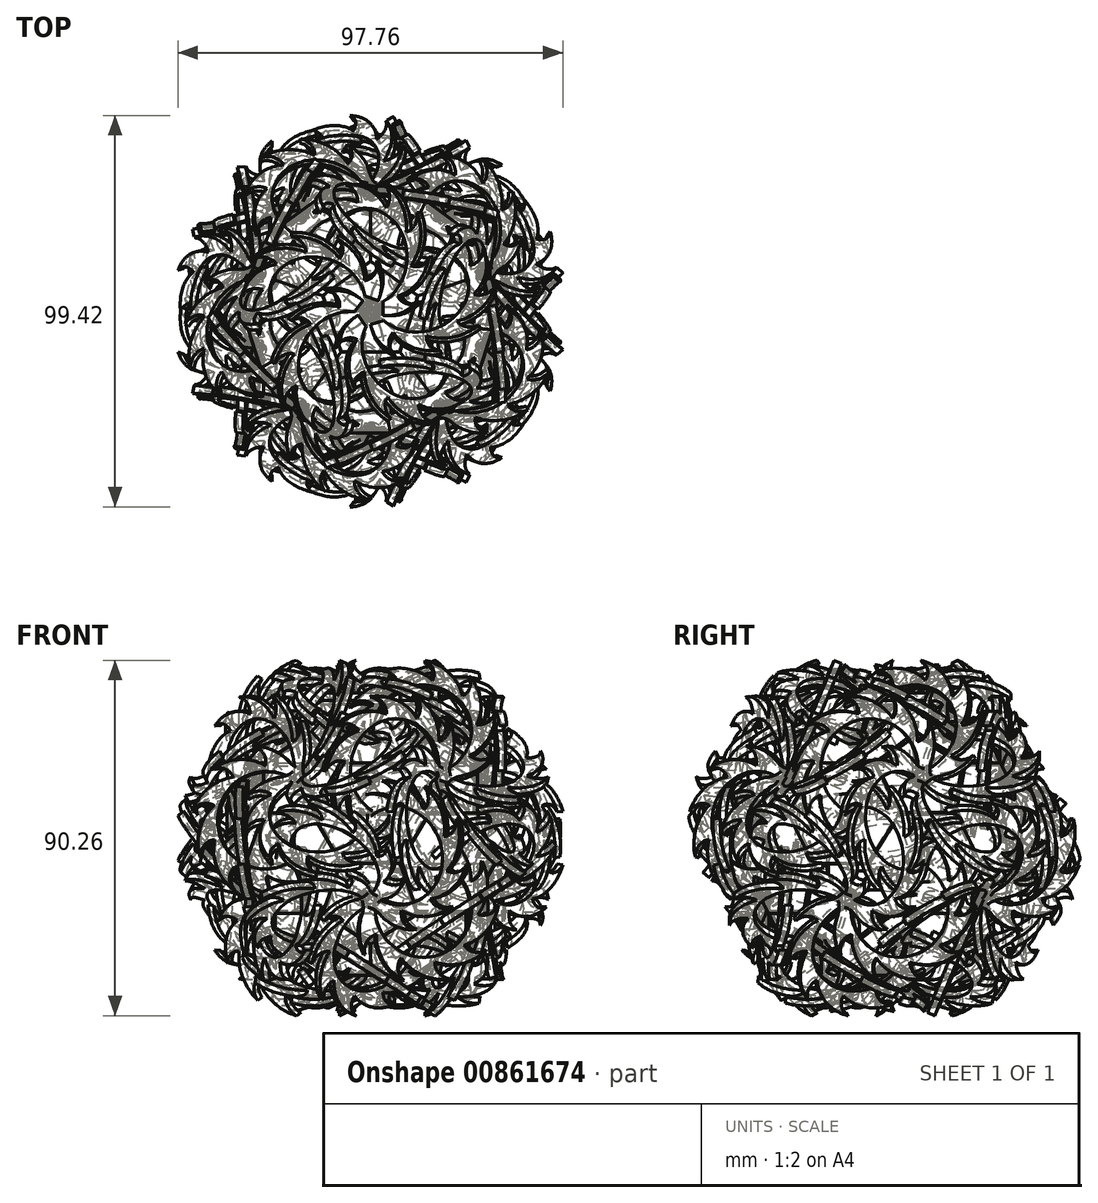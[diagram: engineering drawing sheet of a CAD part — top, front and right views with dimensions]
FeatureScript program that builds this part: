
annotation { "Feature Type Name" : "Feature", "Feature Type Description" : "" }
export const myFeature = defineFeature(function(context is Context, id is Id, definition is map)
    precondition{}
    {
        {
            var Q0;
            Q0=qCreatedBy(makeId("Top.planeOp"),FACE);
            var sketch = newSketch(context, id + "F0", { "sketchPlane" : qUnion([Q0])});
            skCircle(sketch, "E0.cCircle", {"center": v(0, 0) * mm, "radius": 10.32 * mm, "construction": true});
            skLineSegment(sketch, "E0.0", {"start": v(7.5, -10.32) * mm, "end": v(-7.5, -10.32) * mm});
            skLineSegment(sketch, "E0.1", {"start": v(-7.5, -10.32) * mm, "end": v(-12.14, 3.94) * mm});
            skLineSegment(sketch, "E0.2", {"start": v(-12.14, 3.94) * mm, "end": v(0, 12.76) * mm});
            skLineSegment(sketch, "E0.3", {"start": v(0, 12.76) * mm, "end": v(12.14, 3.94) * mm});
            skLineSegment(sketch, "E0.4", {"start": v(12.14, 3.94) * mm, "end": v(7.5, -10.32) * mm});
            skPoint(sketch, "E0.0.midPoint", {"position": v(0, -10.32) * mm});
            skLineSegment(sketch, "E1", {"start": v(0, 12.76) * mm, "end": v(0, -10.32) * mm});
            skSolve(sketch);
        }
        {
            var Q0;
            Q0=qCreatedBy(makeId("Top.planeOp"),FACE);
            var sketch = newSketch(context, id + "F1", { "sketchPlane" : qUnion([Q0])});
            skCircle(sketch, "E2.cCircle", {"center": v(22.17, -7.2) * mm, "radius": 13 * mm, "construction": true});
            skLineSegment(sketch, "E2.0", {"start": v(36.84, -4.09) * mm, "end": v(32.2, -18.35) * mm});
            skLineSegment(sketch, "E2.1", {"start": v(32.2, -18.35) * mm, "end": v(17.54, -21.47) * mm});
            skLineSegment(sketch, "E2.2", {"start": v(17.54, -21.47) * mm, "end": v(7.5, -10.32) * mm});
            skLineSegment(sketch, "E2.3", {"start": v(7.5, -10.32) * mm, "end": v(12.14, 3.94) * mm});
            skLineSegment(sketch, "E2.4", {"start": v(12.14, 3.94) * mm, "end": v(26.8, 7.06) * mm});
            skLineSegment(sketch, "E2.5", {"start": v(26.8, 7.06) * mm, "end": v(36.84, -4.09) * mm});
            skPoint(sketch, "E2.0.midPoint", {"position": v(34.53, -11.22) * mm});
            skSolve(sketch);
        }
        {
            var Q0;
            Q0=makeQuery(id+"F0.imprint","IMPRINT",FACE,{"disambiguationData":[TD([[makeQuery(id+"F0.imprint","IMPRINT",EDGE,{"derivedFrom":sQuery(id+"F0.wireOp",EDGE,"E0.0")}),-1.0]])]});
            extrude(context, id + "F2", {"entities" : qUnion([Q0]), "oppositeDirection" : true, "depth" : 1 * mm});
        }
        {
            var Q0;
            Q0=makeQuery(id+"F1.imprint","IMPRINT",FACE,{"disambiguationData":[TD([[makeQuery(id+"F1.imprint","IMPRINT",EDGE,{"derivedFrom":sQuery(id+"F1.wireOp",EDGE,"E2.0")}),-1.0]])]});
            extrude(context, id + "F3", {"entities" : qUnion([Q0]), "oppositeDirection" : true, "depth" : 1 * mm});
        }
        {
            var Q0;
            Q0=makeQuery(id+"F3.opExtrude","SWEPT_BODY",BODY,{"disambiguationData":[OSD([sQuery(id+"F1.wireOp",EDGE,"E2.0"),sQuery(id+"F1.wireOp",EDGE,"E2.1"),sQuery(id+"F1.wireOp",EDGE,"E2.2"),sQuery(id+"F1.wireOp",EDGE,"E2.3"),sQuery(id+"F1.wireOp",EDGE,"E2.4"),sQuery(id+"F1.wireOp",EDGE,"E2.5")])]});
            var Q1;
            Q1=makeQuery(id+"F2.opExtrude","CAP_EDGE",EDGE,{"disambiguationData":[OSD([sQuery(id+"F0.wireOp",EDGE,"E0.4")])],"isStart":true});
            transform(context, id + "F4", {"entities" : qUnion([Q0]), "transformType" : TransformType.ROTATION, "transformAxis" : qUnion([Q1]), "angle" : 37.38 * degree, "oppositeDirection" : true, "makeCopy" : false});
        }
        {
            var Q0;
            Q0=qCreatedBy(makeId("Right.planeOp"),FACE);
            var sketch = newSketch(context, id + "F5", { "sketchPlane" : qUnion([Q0])});
            skLineSegment(sketch, "E3", {"start": v(0, 0) * mm, "end": v(0, 7.73) * mm});
            skSolve(sketch);
        }
        {
            var Q0;
            Q0=makeQuery(id+"F3.opExtrude","SWEPT_BODY",BODY,{"disambiguationData":[OSD([sQuery(id+"F1.wireOp",EDGE,"E2.0"),sQuery(id+"F1.wireOp",EDGE,"E2.1"),sQuery(id+"F1.wireOp",EDGE,"E2.2"),sQuery(id+"F1.wireOp",EDGE,"E2.3"),sQuery(id+"F1.wireOp",EDGE,"E2.4"),sQuery(id+"F1.wireOp",EDGE,"E2.5")])]});
            var Q1;
            Q1=sQuery(id+"F5.wireOp",EDGE,"E3");
            circularPattern(context, id + "F6", {"entities" : qUnion([Q0]), "axis" : qUnion([Q1]), "angle" : 72 * degree, "instanceCount" : round(5)});
        }
        {
            var Q0;
            Q0=makeQuery(id+"F6.opPattern","COPY",FACE,{"derivedFrom":makeQuery(id+"F3.opExtrude","CAP_FACE",FACE,{"disambiguationData":[OSD([sQuery(id+"F1.wireOp",EDGE,"E2.0"),sQuery(id+"F1.wireOp",EDGE,"E2.1"),sQuery(id+"F1.wireOp",EDGE,"E2.2"),sQuery(id+"F1.wireOp",EDGE,"E2.3"),sQuery(id+"F1.wireOp",EDGE,"E2.4"),sQuery(id+"F1.wireOp",EDGE,"E2.5")])],"isStart":true}),"instanceName":"4"});
            var sketch = newSketch(context, id + "F7", { "sketchPlane" : qUnion([Q0])});
            skLineSegment(sketch, "E4", {"start": v(0, -34.18) * mm, "end": v(0, -8.2) * mm});
            skLineSegment(sketch, "E5", {"start": v(-15, -21.2) * mm, "end": v(15, -21.2) * mm});
            skCircle(sketch, "E6", {"center": v(0, -21.2) * mm, "radius": 3.24 * mm});
            skSolve(sketch);
        }
        {
            var Q0;
            Q0=qCreatedBy(makeId("Right.planeOp"),FACE);
            var sketch = newSketch(context, id + "F8", { "sketchPlane" : qUnion([Q0])});
            skArc(sketch, "E7.0", {"start": v(-1.37, 0) * mm, "mid": v(-18.04, 14.75) * mm, "end": v(-20.04, -7.42) * mm});
            skLineSegment(sketch, "E8", {"start": v(-20.04, -7.42) * mm, "end": v(-24.47, -10.8) * mm});
            skLineSegment(sketch, "E9", {"start": v(-1.37, 0) * mm, "end": v(0, 0) * mm});
            skArc(sketch, "E10", {"start": v(1.07, 1.27) * mm, "mid": v(3.46, 7.37) * mm, "end": v(2.5, 13.85) * mm});
            skArc(sketch, "E11", {"start": v(-0.8, 8.97) * mm, "mid": v(1.84, 10.74) * mm, "end": v(2.5, 13.85) * mm});
            skArc(sketch, "E12.1.0", {"start": v(-0.8, 8.97) * mm, "mid": v(-2.13, 15.94) * mm, "end": v(-6.98, 21.1) * mm});
            skArc(sketch, "E12.1.1", {"start": v(-6.75, 15.32) * mm, "mid": v(-5.72, 18.26) * mm, "end": v(-6.98, 21.1) * mm});
            skArc(sketch, "E12.2.0", {"start": v(-6.75, 15.32) * mm, "mid": v(-11.92, 20.18) * mm, "end": v(-18.89, 21.5) * mm});
            skArc(sketch, "E12.2.1", {"start": v(-15.3, 16.96) * mm, "mid": v(-16.2, 19.94) * mm, "end": v(-18.89, 21.5) * mm});
            skArc(sketch, "E12.3.0", {"start": v(-15.3, 16.96) * mm, "mid": v(-22.34, 17.85) * mm, "end": v(-28.75, 14.83) * mm});
            skArc(sketch, "E12.3.1", {"start": v(-23.18, 13.26) * mm, "mid": v(-25.66, 15.15) * mm, "end": v(-28.75, 14.83) * mm});
            skArc(sketch, "E12.4.0", {"start": v(-23.18, 13.26) * mm, "mid": v(-29.4, 9.84) * mm, "end": v(-32.81, 3.63) * mm});
            skArc(sketch, "E12.4.1", {"start": v(-27.38, 5.64) * mm, "mid": v(-30.5, 5.7) * mm, "end": v(-32.81, 3.63) * mm});
            skArc(sketch, "E12.5.0", {"start": v(-27.38, 5.64) * mm, "mid": v(-30.4, -0.78) * mm, "end": v(-29.51, -7.81) * mm});
            skArc(sketch, "E12.5.1", {"start": v(-26.3, -3) * mm, "mid": v(-28.86, -4.77) * mm, "end": v(-29.51, -7.81) * mm});
            skArc(sketch, "E12.6.0", {"start": v(-26.3, -3) * mm, "mid": v(-26.03, -7.06) * mm, "end": v(-24.49, -10.82) * mm});
            skArc(sketch, "E13", {"start": v(-24.49, -10.82) * mm, "mid": v(-20.56, -11.35) * mm, "end": v(-20.04, -7.42) * mm});
            skArc(sketch, "E14", {"start": v(-1.37, 0) * mm, "mid": v(1.27, -2.11) * mm, "end": v(1.07, 1.27) * mm});
            skSolve(sketch);
        }
        {
            var Q0;
            {var subQ2=sQuery(id+"F8.wireOp",EDGE,"E7.0");Q0=makeQuery(id+"F8.imprint","IMPRINT",FACE,{"disambiguationData":[TD([[makeQuery(id+"F8.imprint","IMPRINT",EDGE,{"derivedFrom":subQ2}),-1.0]])]});}
            extrude(context, id + "F9", {"entities" : qUnion([Q0]), "oppositeDirection" : true, "depth" : 2 * mm});
        }
        {
            var Q0;
            Q0=makeQuery(id+"F9.opExtrude","SWEPT_EDGE",EDGE,{"disambiguationData":[OSD([sQuery(id+"F8.wireOp",EDGE,"E10"),sQuery(id+"F8.wireOp",EDGE,"E14")])]});
            fillet(context, id + "F10", {"entities" : qUnion([Q0]), "radius" : 5 * mm, "tangentPropagation" : true, "allowEdgeOverflow" : false});
        }
        {
            var Q0;
            Q0=qCreatedBy(makeId("Right.planeOp"),FACE);
            var sketch = newSketch(context, id + "F11", { "sketchPlane" : qUnion([Q0])});
            skLineSegment(sketch, "E15", {"start": v(0, 0) * mm, "end": v(-20.65, -7.89) * mm});
            skLineSegment(sketch, "E16", {"start": v(0, 0) * mm, "end": v(0, 28.42) * mm});
            skSolve(sketch);
        }
        {
            var Q0;
            Q0=makeQuery(id+"F9.opExtrude","SWEPT_BODY",BODY,{"disambiguationData":[OSD([sQuery(id+"F8.wireOp",EDGE,"003f2e54-bd62-4f0b-a98e-8c36e71e2cf6"),sQuery(id+"F8.wireOp",EDGE,"8c729305-40a1-49fa-b790-4b99a3909bb6"),sQuery(id+"F8.wireOp",EDGE,"862a2a8f-3db7-4421-9c69-6ab2f53c4c24.1.0"),sQuery(id+"F8.wireOp",EDGE,"862a2a8f-3db7-4421-9c69-6ab2f53c4c24.1.1"),sQuery(id+"F8.wireOp",EDGE,"862a2a8f-3db7-4421-9c69-6ab2f53c4c24.2.0"),sQuery(id+"F8.wireOp",EDGE,"862a2a8f-3db7-4421-9c69-6ab2f53c4c24.2.1"),sQuery(id+"F8.wireOp",EDGE,"862a2a8f-3db7-4421-9c69-6ab2f53c4c24.3.0"),sQuery(id+"F8.wireOp",EDGE,"862a2a8f-3db7-4421-9c69-6ab2f53c4c24.3.1"),sQuery(id+"F8.wireOp",EDGE,"862a2a8f-3db7-4421-9c69-6ab2f53c4c24.4.0"),sQuery(id+"F8.wireOp",EDGE,"862a2a8f-3db7-4421-9c69-6ab2f53c4c24.4.1"),sQuery(id+"F8.wireOp",EDGE,"862a2a8f-3db7-4421-9c69-6ab2f53c4c24.5.0"),sQuery(id+"F8.wireOp",EDGE,"E7.0"),sQuery(id+"F8.wireOp",EDGE,"E8"),sQuery(id+"F8.wireOp",EDGE,"E9")])]});
            var Q1;
            Q1=sQuery(id+"F11.wireOp",EDGE,"E15");
            transform(context, id + "F12", {"entities" : qUnion([Q0]), "transformType" : TransformType.ROTATION, "transformAxis" : qUnion([Q1]), "angle" : 65 * degree, "makeCopy" : false});
        }
        {
            var Q0;
            Q0=makeQuery(id+"F9.opExtrude","SWEPT_BODY",BODY,{"disambiguationData":[OSD([sQuery(id+"F8.wireOp",EDGE,"003f2e54-bd62-4f0b-a98e-8c36e71e2cf6"),sQuery(id+"F8.wireOp",EDGE,"8c729305-40a1-49fa-b790-4b99a3909bb6"),sQuery(id+"F8.wireOp",EDGE,"862a2a8f-3db7-4421-9c69-6ab2f53c4c24.1.0"),sQuery(id+"F8.wireOp",EDGE,"862a2a8f-3db7-4421-9c69-6ab2f53c4c24.1.1"),sQuery(id+"F8.wireOp",EDGE,"862a2a8f-3db7-4421-9c69-6ab2f53c4c24.2.0"),sQuery(id+"F8.wireOp",EDGE,"862a2a8f-3db7-4421-9c69-6ab2f53c4c24.2.1"),sQuery(id+"F8.wireOp",EDGE,"862a2a8f-3db7-4421-9c69-6ab2f53c4c24.3.0"),sQuery(id+"F8.wireOp",EDGE,"862a2a8f-3db7-4421-9c69-6ab2f53c4c24.3.1"),sQuery(id+"F8.wireOp",EDGE,"862a2a8f-3db7-4421-9c69-6ab2f53c4c24.4.0"),sQuery(id+"F8.wireOp",EDGE,"862a2a8f-3db7-4421-9c69-6ab2f53c4c24.4.1"),sQuery(id+"F8.wireOp",EDGE,"862a2a8f-3db7-4421-9c69-6ab2f53c4c24.5.0"),sQuery(id+"F8.wireOp",EDGE,"E7.0"),sQuery(id+"F8.wireOp",EDGE,"E8"),sQuery(id+"F8.wireOp",EDGE,"E9")])]});
            var Q1;
            Q1=sQuery(id+"F11.wireOp",EDGE,"E16");
            circularPattern(context, id + "F13", {"entities" : qUnion([Q0]), "axis" : qUnion([Q1]), "angle" : 72 * degree, "instanceCount" : round(5)});
        }
        {
            var Q0;
            Q0=qCreatedBy(makeId("Right.planeOp"),FACE);
            var sketch = newSketch(context, id + "F14", { "sketchPlane" : qUnion([Q0])});
            skLineSegment(sketch, "E17.0", {"start": v(-30.97, -15.77) * mm, "end": v(-10.32, 0) * mm});
            skLineSegment(sketch, "E18", {"start": v(-20.65, -7.89) * mm, "end": v(-30.05, 4.42) * mm});
            skSolve(sketch);
        }
        {
            var Q0;
            Q0=makeQuery(id+"F9.opExtrude","SWEPT_BODY",BODY,{"disambiguationData":[OSD([sQuery(id+"F8.wireOp",EDGE,"003f2e54-bd62-4f0b-a98e-8c36e71e2cf6"),sQuery(id+"F8.wireOp",EDGE,"8c729305-40a1-49fa-b790-4b99a3909bb6"),sQuery(id+"F8.wireOp",EDGE,"862a2a8f-3db7-4421-9c69-6ab2f53c4c24.1.0"),sQuery(id+"F8.wireOp",EDGE,"862a2a8f-3db7-4421-9c69-6ab2f53c4c24.1.1"),sQuery(id+"F8.wireOp",EDGE,"862a2a8f-3db7-4421-9c69-6ab2f53c4c24.2.0"),sQuery(id+"F8.wireOp",EDGE,"862a2a8f-3db7-4421-9c69-6ab2f53c4c24.2.1"),sQuery(id+"F8.wireOp",EDGE,"862a2a8f-3db7-4421-9c69-6ab2f53c4c24.3.0"),sQuery(id+"F8.wireOp",EDGE,"862a2a8f-3db7-4421-9c69-6ab2f53c4c24.3.1"),sQuery(id+"F8.wireOp",EDGE,"862a2a8f-3db7-4421-9c69-6ab2f53c4c24.4.0"),sQuery(id+"F8.wireOp",EDGE,"862a2a8f-3db7-4421-9c69-6ab2f53c4c24.4.1"),sQuery(id+"F8.wireOp",EDGE,"862a2a8f-3db7-4421-9c69-6ab2f53c4c24.5.0"),sQuery(id+"F8.wireOp",EDGE,"E7.0"),sQuery(id+"F8.wireOp",EDGE,"E8"),sQuery(id+"F8.wireOp",EDGE,"E9")])]});
            var Q1;
            Q1=sQuery(id+"F14.wireOp",EDGE,"E18");
            circularPattern(context, id + "F15", {"entities" : qUnion([Q0]), "axis" : qUnion([Q1]), "angle" : 120 * degree, "instanceCount" : round(3)});
        }
        {
            var Q0;
            Q0=makeQuery(id+"F15.opPattern","COPY",BODY,{"derivedFrom":makeQuery(id+"F9.opExtrude","SWEPT_BODY",BODY,{"disambiguationData":[OSD([sQuery(id+"F8.wireOp",EDGE,"E7.0"),sQuery(id+"F8.wireOp",EDGE,"E10"),sQuery(id+"F8.wireOp",EDGE,"E11"),sQuery(id+"F8.wireOp",EDGE,"E12.1.0"),sQuery(id+"F8.wireOp",EDGE,"E12.1.1"),sQuery(id+"F8.wireOp",EDGE,"E12.2.0"),sQuery(id+"F8.wireOp",EDGE,"E12.2.1"),sQuery(id+"F8.wireOp",EDGE,"E12.3.0"),sQuery(id+"F8.wireOp",EDGE,"E12.3.1"),sQuery(id+"F8.wireOp",EDGE,"E12.4.0"),sQuery(id+"F8.wireOp",EDGE,"E12.4.1"),sQuery(id+"F8.wireOp",EDGE,"E12.5.0"),sQuery(id+"F8.wireOp",EDGE,"E12.5.1"),sQuery(id+"F8.wireOp",EDGE,"E12.6.0"),sQuery(id+"F8.wireOp",EDGE,"E13"),sQuery(id+"F8.wireOp",EDGE,"E14")])]}),"instanceName":"2"});
            var Q1;
            Q1=makeQuery(id+"F15.opPattern","COPY",BODY,{"derivedFrom":makeQuery(id+"F9.opExtrude","SWEPT_BODY",BODY,{"disambiguationData":[OSD([sQuery(id+"F8.wireOp",EDGE,"E7.0"),sQuery(id+"F8.wireOp",EDGE,"E10"),sQuery(id+"F8.wireOp",EDGE,"E11"),sQuery(id+"F8.wireOp",EDGE,"E12.1.0"),sQuery(id+"F8.wireOp",EDGE,"E12.1.1"),sQuery(id+"F8.wireOp",EDGE,"E12.2.0"),sQuery(id+"F8.wireOp",EDGE,"E12.2.1"),sQuery(id+"F8.wireOp",EDGE,"E12.3.0"),sQuery(id+"F8.wireOp",EDGE,"E12.3.1"),sQuery(id+"F8.wireOp",EDGE,"E12.4.0"),sQuery(id+"F8.wireOp",EDGE,"E12.4.1"),sQuery(id+"F8.wireOp",EDGE,"E12.5.0"),sQuery(id+"F8.wireOp",EDGE,"E12.5.1"),sQuery(id+"F8.wireOp",EDGE,"E12.6.0"),sQuery(id+"F8.wireOp",EDGE,"E13"),sQuery(id+"F8.wireOp",EDGE,"E14")])]}),"instanceName":"1"});
            var Q2;
            Q2=sQuery(id+"F11.wireOp",EDGE,"E16");
            circularPattern(context, id + "F16", {"entities" : qUnion([Q0, Q1]), "axis" : qUnion([Q2]), "angle" : 72 * degree, "instanceCount" : round(5)});
        }
        {
            var Q0;
            Q0=makeQuery(id+"F3.opExtrude","SWEPT_BODY",BODY,{"disambiguationData":[OSD([sQuery(id+"F1.wireOp",EDGE,"E2.0"),sQuery(id+"F1.wireOp",EDGE,"E2.1"),sQuery(id+"F1.wireOp",EDGE,"E2.2"),sQuery(id+"F1.wireOp",EDGE,"E2.3"),sQuery(id+"F1.wireOp",EDGE,"E2.4"),sQuery(id+"F1.wireOp",EDGE,"E2.5")])]});
            var Q1;
            Q1=makeQuery(id+"F16.opPattern","COPY",BODY,{"derivedFrom":makeQuery(id+"F15.opPattern","COPY",BODY,{"derivedFrom":makeQuery(id+"F9.opExtrude","SWEPT_BODY",BODY,{"disambiguationData":[OSD([sQuery(id+"F8.wireOp",EDGE,"E7.0"),sQuery(id+"F8.wireOp",EDGE,"E10"),sQuery(id+"F8.wireOp",EDGE,"E11"),sQuery(id+"F8.wireOp",EDGE,"E12.1.0"),sQuery(id+"F8.wireOp",EDGE,"E12.1.1"),sQuery(id+"F8.wireOp",EDGE,"E12.2.0"),sQuery(id+"F8.wireOp",EDGE,"E12.2.1"),sQuery(id+"F8.wireOp",EDGE,"E12.3.0"),sQuery(id+"F8.wireOp",EDGE,"E12.3.1"),sQuery(id+"F8.wireOp",EDGE,"E12.4.0"),sQuery(id+"F8.wireOp",EDGE,"E12.4.1"),sQuery(id+"F8.wireOp",EDGE,"E12.5.0"),sQuery(id+"F8.wireOp",EDGE,"E12.5.1"),sQuery(id+"F8.wireOp",EDGE,"E12.6.0"),sQuery(id+"F8.wireOp",EDGE,"E13"),sQuery(id+"F8.wireOp",EDGE,"E14")])]}),"instanceName":"1"}),"instanceName":"1"});
            var Q2;
            Q2=makeQuery(id+"F13.opPattern","COPY",BODY,{"derivedFrom":makeQuery(id+"F9.opExtrude","SWEPT_BODY",BODY,{"disambiguationData":[OSD([sQuery(id+"F8.wireOp",EDGE,"E7.0"),sQuery(id+"F8.wireOp",EDGE,"E10"),sQuery(id+"F8.wireOp",EDGE,"E11"),sQuery(id+"F8.wireOp",EDGE,"E12.1.0"),sQuery(id+"F8.wireOp",EDGE,"E12.1.1"),sQuery(id+"F8.wireOp",EDGE,"E12.2.0"),sQuery(id+"F8.wireOp",EDGE,"E12.2.1"),sQuery(id+"F8.wireOp",EDGE,"E12.3.0"),sQuery(id+"F8.wireOp",EDGE,"E12.3.1"),sQuery(id+"F8.wireOp",EDGE,"E12.4.0"),sQuery(id+"F8.wireOp",EDGE,"E12.4.1"),sQuery(id+"F8.wireOp",EDGE,"E12.5.0"),sQuery(id+"F8.wireOp",EDGE,"E12.5.1"),sQuery(id+"F8.wireOp",EDGE,"E12.6.0"),sQuery(id+"F8.wireOp",EDGE,"E13"),sQuery(id+"F8.wireOp",EDGE,"E14")])]}),"instanceName":"1"});
            var Q3;
            Q3=makeQuery(id+"F16.opPattern","COPY",BODY,{"derivedFrom":makeQuery(id+"F15.opPattern","COPY",BODY,{"derivedFrom":makeQuery(id+"F9.opExtrude","SWEPT_BODY",BODY,{"disambiguationData":[OSD([sQuery(id+"F8.wireOp",EDGE,"E7.0"),sQuery(id+"F8.wireOp",EDGE,"E10"),sQuery(id+"F8.wireOp",EDGE,"E11"),sQuery(id+"F8.wireOp",EDGE,"E12.1.0"),sQuery(id+"F8.wireOp",EDGE,"E12.1.1"),sQuery(id+"F8.wireOp",EDGE,"E12.2.0"),sQuery(id+"F8.wireOp",EDGE,"E12.2.1"),sQuery(id+"F8.wireOp",EDGE,"E12.3.0"),sQuery(id+"F8.wireOp",EDGE,"E12.3.1"),sQuery(id+"F8.wireOp",EDGE,"E12.4.0"),sQuery(id+"F8.wireOp",EDGE,"E12.4.1"),sQuery(id+"F8.wireOp",EDGE,"E12.5.0"),sQuery(id+"F8.wireOp",EDGE,"E12.5.1"),sQuery(id+"F8.wireOp",EDGE,"E12.6.0"),sQuery(id+"F8.wireOp",EDGE,"E13"),sQuery(id+"F8.wireOp",EDGE,"E14")])]}),"instanceName":"2"}),"instanceName":"1"});
            var Q4;
            Q4=sQuery(id+"F14.wireOp",EDGE,"E18");
            circularPattern(context, id + "F17", {"entities" : qUnion([Q0, Q1, Q2, Q3]), "axis" : qUnion([Q4]), "angle" : 120 * degree, "instanceCount" : 2, "oppositeDirection" : true});
        }
        {
            var Q0;
            Q0=makeQuery(id+"F2.opExtrude","SWEPT_BODY",BODY,{"disambiguationData":[OSD([sQuery(id+"F0.wireOp",EDGE,"E0.0"),sQuery(id+"F0.wireOp",EDGE,"E0.1"),sQuery(id+"F0.wireOp",EDGE,"E0.2"),sQuery(id+"F0.wireOp",EDGE,"E0.3"),sQuery(id+"F0.wireOp",EDGE,"E0.4")])]});
            var Q1;
            Q1=makeQuery(id+"F13.opPattern","COPY",BODY,{"derivedFrom":makeQuery(id+"F9.opExtrude","SWEPT_BODY",BODY,{"disambiguationData":[OSD([sQuery(id+"F8.wireOp",EDGE,"E7.0"),sQuery(id+"F8.wireOp",EDGE,"E10"),sQuery(id+"F8.wireOp",EDGE,"E11"),sQuery(id+"F8.wireOp",EDGE,"E12.1.0"),sQuery(id+"F8.wireOp",EDGE,"E12.1.1"),sQuery(id+"F8.wireOp",EDGE,"E12.2.0"),sQuery(id+"F8.wireOp",EDGE,"E12.2.1"),sQuery(id+"F8.wireOp",EDGE,"E12.3.0"),sQuery(id+"F8.wireOp",EDGE,"E12.3.1"),sQuery(id+"F8.wireOp",EDGE,"E12.4.0"),sQuery(id+"F8.wireOp",EDGE,"E12.4.1"),sQuery(id+"F8.wireOp",EDGE,"E12.5.0"),sQuery(id+"F8.wireOp",EDGE,"E12.5.1"),sQuery(id+"F8.wireOp",EDGE,"E12.6.0"),sQuery(id+"F8.wireOp",EDGE,"E13"),sQuery(id+"F8.wireOp",EDGE,"E14")])]}),"instanceName":"2"});
            var Q2;
            Q2=makeQuery(id+"F13.opPattern","COPY",BODY,{"derivedFrom":makeQuery(id+"F9.opExtrude","SWEPT_BODY",BODY,{"disambiguationData":[OSD([sQuery(id+"F8.wireOp",EDGE,"E7.0"),sQuery(id+"F8.wireOp",EDGE,"E10"),sQuery(id+"F8.wireOp",EDGE,"E11"),sQuery(id+"F8.wireOp",EDGE,"E12.1.0"),sQuery(id+"F8.wireOp",EDGE,"E12.1.1"),sQuery(id+"F8.wireOp",EDGE,"E12.2.0"),sQuery(id+"F8.wireOp",EDGE,"E12.2.1"),sQuery(id+"F8.wireOp",EDGE,"E12.3.0"),sQuery(id+"F8.wireOp",EDGE,"E12.3.1"),sQuery(id+"F8.wireOp",EDGE,"E12.4.0"),sQuery(id+"F8.wireOp",EDGE,"E12.4.1"),sQuery(id+"F8.wireOp",EDGE,"E12.5.0"),sQuery(id+"F8.wireOp",EDGE,"E12.5.1"),sQuery(id+"F8.wireOp",EDGE,"E12.6.0"),sQuery(id+"F8.wireOp",EDGE,"E13"),sQuery(id+"F8.wireOp",EDGE,"E14")])]}),"instanceName":"3"});
            var Q3;
            Q3=sQuery(id+"F14.wireOp",EDGE,"E18");
            circularPattern(context, id + "F18", {"entities" : qUnion([Q0, Q1, Q2]), "axis" : qUnion([Q3]), "angle" : 120 * degree, "instanceCount" : round(3)});
        }
        {
            var Q0;
            Q0=makeQuery(id+"F18.opPattern","COPY",FACE,{"derivedFrom":makeQuery(id+"F2.opExtrude","CAP_FACE",FACE,{"disambiguationData":[OSD([sQuery(id+"F0.wireOp",EDGE,"E0.0"),sQuery(id+"F0.wireOp",EDGE,"E0.1"),sQuery(id+"F0.wireOp",EDGE,"E0.2"),sQuery(id+"F0.wireOp",EDGE,"E0.3"),sQuery(id+"F0.wireOp",EDGE,"E0.4")])],"isStart":true}),"instanceName":"1"});
            var sketch = newSketch(context, id + "F19", { "sketchPlane" : qUnion([Q0])});
            skLineSegment(sketch, "E19", {"start": v(-1.3, -23.63) * mm, "end": v(-19.97, -37.2) * mm});
            skLineSegment(sketch, "E20", {"start": v(-19.97, -22.2) * mm, "end": v(-1.3, -35.77) * mm});
            skSolve(sketch);
        }
        {
            var Q0;
            Q0=sQuery(id+"F19.wireOp",VERTEX,"E19.end");
            var Q1;
            Q1=sQuery(id+"F19.wireOp",VERTEX,"E19.start");
            var Q2;
            Q2=sQuery(id+"F14.wireOp",VERTEX,"E18.end");
            cPlane(context, id + "F20", {"entities" : qUnion([Q0, Q1, Q2]), "cplaneType" : CPlaneType.THREE_POINT, "offset" : 150 * mm, "width" : 150 * mm, "height" : 150 * mm});
        }
        {
            var Q0;
            Q0=qCreatedBy(id+"F20.planeOp",FACE);
            var sketch = newSketch(context, id + "F21", { "sketchPlane" : qUnion([Q0])});
            skLineSegment(sketch, "E21.0", {"start": v(23.59, 6.27) * mm, "end": v(41.93, -7.75) * mm});
            skLineSegment(sketch, "E21.1", {"start": v(34.92, -2.4) * mm, "end": v(29.26, 1.94) * mm});
            skLineSegment(sketch, "E22", {"start": v(31.8, 0) * mm, "end": v(33.22, 1.87) * mm});
            skLineSegment(sketch, "E23", {"start": v(33.22, 1.87) * mm, "end": v(37.58, 7.58) * mm});
            skSolve(sketch);
        }
        {
            var Q0;
            Q0=makeQuery(id+"F17.opPattern","COPY",BODY,{"derivedFrom":makeQuery(id+"F3.opExtrude","SWEPT_BODY",BODY,{"disambiguationData":[OSD([sQuery(id+"F1.wireOp",EDGE,"E2.0"),sQuery(id+"F1.wireOp",EDGE,"E2.1"),sQuery(id+"F1.wireOp",EDGE,"E2.2"),sQuery(id+"F1.wireOp",EDGE,"E2.3"),sQuery(id+"F1.wireOp",EDGE,"E2.4"),sQuery(id+"F1.wireOp",EDGE,"E2.5")])]}),"instanceName":"1"});
            var Q1;
            Q1=makeQuery(id+"F17.opPattern","COPY",BODY,{"derivedFrom":makeQuery(id+"F13.opPattern","COPY",BODY,{"derivedFrom":makeQuery(id+"F9.opExtrude","SWEPT_BODY",BODY,{"disambiguationData":[OSD([sQuery(id+"F8.wireOp",EDGE,"E7.0"),sQuery(id+"F8.wireOp",EDGE,"E10"),sQuery(id+"F8.wireOp",EDGE,"E11"),sQuery(id+"F8.wireOp",EDGE,"E12.1.0"),sQuery(id+"F8.wireOp",EDGE,"E12.1.1"),sQuery(id+"F8.wireOp",EDGE,"E12.2.0"),sQuery(id+"F8.wireOp",EDGE,"E12.2.1"),sQuery(id+"F8.wireOp",EDGE,"E12.3.0"),sQuery(id+"F8.wireOp",EDGE,"E12.3.1"),sQuery(id+"F8.wireOp",EDGE,"E12.4.0"),sQuery(id+"F8.wireOp",EDGE,"E12.4.1"),sQuery(id+"F8.wireOp",EDGE,"E12.5.0"),sQuery(id+"F8.wireOp",EDGE,"E12.5.1"),sQuery(id+"F8.wireOp",EDGE,"E12.6.0"),sQuery(id+"F8.wireOp",EDGE,"E13"),sQuery(id+"F8.wireOp",EDGE,"E14")])]}),"instanceName":"1"}),"instanceName":"1"});
            var Q2;
            Q2=makeQuery(id+"F17.opPattern","COPY",BODY,{"derivedFrom":makeQuery(id+"F16.opPattern","COPY",BODY,{"derivedFrom":makeQuery(id+"F15.opPattern","COPY",BODY,{"derivedFrom":makeQuery(id+"F9.opExtrude","SWEPT_BODY",BODY,{"disambiguationData":[OSD([sQuery(id+"F8.wireOp",EDGE,"E7.0"),sQuery(id+"F8.wireOp",EDGE,"E10"),sQuery(id+"F8.wireOp",EDGE,"E11"),sQuery(id+"F8.wireOp",EDGE,"E12.1.0"),sQuery(id+"F8.wireOp",EDGE,"E12.1.1"),sQuery(id+"F8.wireOp",EDGE,"E12.2.0"),sQuery(id+"F8.wireOp",EDGE,"E12.2.1"),sQuery(id+"F8.wireOp",EDGE,"E12.3.0"),sQuery(id+"F8.wireOp",EDGE,"E12.3.1"),sQuery(id+"F8.wireOp",EDGE,"E12.4.0"),sQuery(id+"F8.wireOp",EDGE,"E12.4.1"),sQuery(id+"F8.wireOp",EDGE,"E12.5.0"),sQuery(id+"F8.wireOp",EDGE,"E12.5.1"),sQuery(id+"F8.wireOp",EDGE,"E12.6.0"),sQuery(id+"F8.wireOp",EDGE,"E13"),sQuery(id+"F8.wireOp",EDGE,"E14")])]}),"instanceName":"2"}),"instanceName":"1"}),"instanceName":"1"});
            var Q3;
            Q3=makeQuery(id+"F17.opPattern","COPY",BODY,{"derivedFrom":makeQuery(id+"F16.opPattern","COPY",BODY,{"derivedFrom":makeQuery(id+"F15.opPattern","COPY",BODY,{"derivedFrom":makeQuery(id+"F9.opExtrude","SWEPT_BODY",BODY,{"disambiguationData":[OSD([sQuery(id+"F8.wireOp",EDGE,"E7.0"),sQuery(id+"F8.wireOp",EDGE,"E10"),sQuery(id+"F8.wireOp",EDGE,"E11"),sQuery(id+"F8.wireOp",EDGE,"E12.1.0"),sQuery(id+"F8.wireOp",EDGE,"E12.1.1"),sQuery(id+"F8.wireOp",EDGE,"E12.2.0"),sQuery(id+"F8.wireOp",EDGE,"E12.2.1"),sQuery(id+"F8.wireOp",EDGE,"E12.3.0"),sQuery(id+"F8.wireOp",EDGE,"E12.3.1"),sQuery(id+"F8.wireOp",EDGE,"E12.4.0"),sQuery(id+"F8.wireOp",EDGE,"E12.4.1"),sQuery(id+"F8.wireOp",EDGE,"E12.5.0"),sQuery(id+"F8.wireOp",EDGE,"E12.5.1"),sQuery(id+"F8.wireOp",EDGE,"E12.6.0"),sQuery(id+"F8.wireOp",EDGE,"E13"),sQuery(id+"F8.wireOp",EDGE,"E14")])]}),"instanceName":"1"}),"instanceName":"1"}),"instanceName":"1"});
            var Q4;
            Q4=sQuery(id+"F21.wireOp",EDGE,"E22");
            circularPattern(context, id + "F22", {"entities" : qUnion([Q0, Q1, Q2, Q3]), "axis" : qUnion([Q4]), "angle" : 72 * degree, "instanceCount" : round(3), "oppositeDirection" : true});
        }
        {
            var Q0;
            Q0=makeQuery(id+"F18.opPattern","COPY",FACE,{"derivedFrom":makeQuery(id+"F2.opExtrude","CAP_FACE",FACE,{"disambiguationData":[OSD([sQuery(id+"F0.wireOp",EDGE,"E0.0"),sQuery(id+"F0.wireOp",EDGE,"E0.1"),sQuery(id+"F0.wireOp",EDGE,"E0.2"),sQuery(id+"F0.wireOp",EDGE,"E0.3"),sQuery(id+"F0.wireOp",EDGE,"E0.4")])],"isStart":true}),"instanceName":"2"});
            var sketch = newSketch(context, id + "F23", { "sketchPlane" : qUnion([Q0])});
            skLineSegment(sketch, "E24", {"start": v(1.3, -23.63) * mm, "end": v(19.97, -37.2) * mm});
            skLineSegment(sketch, "E25", {"start": v(5.7, -41.83) * mm, "end": v(12.84, -19.88) * mm});
            skSolve(sketch);
        }
        {
            var Q0;
            Q0=sQuery(id+"F23.wireOp",VERTEX,"E24.end");
            var Q1;
            Q1=sQuery(id+"F23.wireOp",VERTEX,"E24.start");
            var Q2;
            Q2=sQuery(id+"F14.wireOp",VERTEX,"E18.end");
            cPlane(context, id + "F24", {"entities" : qUnion([Q0, Q1, Q2]), "cplaneType" : CPlaneType.THREE_POINT, "offset" : 150 * mm, "width" : 150 * mm, "height" : 150 * mm});
        }
        {
            var Q0;
            Q0=qCreatedBy(id+"F24.planeOp",FACE);
            var sketch = newSketch(context, id + "F25", { "sketchPlane" : qUnion([Q0])});
            skLineSegment(sketch, "E26.0", {"start": v(23.59, 6.27) * mm, "end": v(41.93, -7.75) * mm});
            skLineSegment(sketch, "E26.1", {"start": v(34.92, -2.4) * mm, "end": v(29.26, 1.94) * mm});
            skLineSegment(sketch, "E27", {"start": v(31.8, 0) * mm, "end": v(36.23, 5.8) * mm});
            skSolve(sketch);
        }
        {
            var Q0;
            Q0=makeQuery(id+"F3.opExtrude","SWEPT_BODY",BODY,{"disambiguationData":[OSD([sQuery(id+"F1.wireOp",EDGE,"E2.0"),sQuery(id+"F1.wireOp",EDGE,"E2.1"),sQuery(id+"F1.wireOp",EDGE,"E2.2"),sQuery(id+"F1.wireOp",EDGE,"E2.3"),sQuery(id+"F1.wireOp",EDGE,"E2.4"),sQuery(id+"F1.wireOp",EDGE,"E2.5")])]});
            var Q1;
            Q1=makeQuery(id+"F16.opPattern","COPY",BODY,{"derivedFrom":makeQuery(id+"F15.opPattern","COPY",BODY,{"derivedFrom":makeQuery(id+"F9.opExtrude","SWEPT_BODY",BODY,{"disambiguationData":[OSD([sQuery(id+"F8.wireOp",EDGE,"E7.0"),sQuery(id+"F8.wireOp",EDGE,"E10"),sQuery(id+"F8.wireOp",EDGE,"E11"),sQuery(id+"F8.wireOp",EDGE,"E12.1.0"),sQuery(id+"F8.wireOp",EDGE,"E12.1.1"),sQuery(id+"F8.wireOp",EDGE,"E12.2.0"),sQuery(id+"F8.wireOp",EDGE,"E12.2.1"),sQuery(id+"F8.wireOp",EDGE,"E12.3.0"),sQuery(id+"F8.wireOp",EDGE,"E12.3.1"),sQuery(id+"F8.wireOp",EDGE,"E12.4.0"),sQuery(id+"F8.wireOp",EDGE,"E12.4.1"),sQuery(id+"F8.wireOp",EDGE,"E12.5.0"),sQuery(id+"F8.wireOp",EDGE,"E12.5.1"),sQuery(id+"F8.wireOp",EDGE,"E12.6.0"),sQuery(id+"F8.wireOp",EDGE,"E13"),sQuery(id+"F8.wireOp",EDGE,"E14")])]}),"instanceName":"2"}),"instanceName":"1"});
            var Q2;
            Q2=makeQuery(id+"F13.opPattern","COPY",BODY,{"derivedFrom":makeQuery(id+"F9.opExtrude","SWEPT_BODY",BODY,{"disambiguationData":[OSD([sQuery(id+"F8.wireOp",EDGE,"E7.0"),sQuery(id+"F8.wireOp",EDGE,"E10"),sQuery(id+"F8.wireOp",EDGE,"E11"),sQuery(id+"F8.wireOp",EDGE,"E12.1.0"),sQuery(id+"F8.wireOp",EDGE,"E12.1.1"),sQuery(id+"F8.wireOp",EDGE,"E12.2.0"),sQuery(id+"F8.wireOp",EDGE,"E12.2.1"),sQuery(id+"F8.wireOp",EDGE,"E12.3.0"),sQuery(id+"F8.wireOp",EDGE,"E12.3.1"),sQuery(id+"F8.wireOp",EDGE,"E12.4.0"),sQuery(id+"F8.wireOp",EDGE,"E12.4.1"),sQuery(id+"F8.wireOp",EDGE,"E12.5.0"),sQuery(id+"F8.wireOp",EDGE,"E12.5.1"),sQuery(id+"F8.wireOp",EDGE,"E12.6.0"),sQuery(id+"F8.wireOp",EDGE,"E13"),sQuery(id+"F8.wireOp",EDGE,"E14")])]}),"instanceName":"1"});
            var Q3;
            Q3=makeQuery(id+"F16.opPattern","COPY",BODY,{"derivedFrom":makeQuery(id+"F15.opPattern","COPY",BODY,{"derivedFrom":makeQuery(id+"F9.opExtrude","SWEPT_BODY",BODY,{"disambiguationData":[OSD([sQuery(id+"F8.wireOp",EDGE,"E7.0"),sQuery(id+"F8.wireOp",EDGE,"E10"),sQuery(id+"F8.wireOp",EDGE,"E11"),sQuery(id+"F8.wireOp",EDGE,"E12.1.0"),sQuery(id+"F8.wireOp",EDGE,"E12.1.1"),sQuery(id+"F8.wireOp",EDGE,"E12.2.0"),sQuery(id+"F8.wireOp",EDGE,"E12.2.1"),sQuery(id+"F8.wireOp",EDGE,"E12.3.0"),sQuery(id+"F8.wireOp",EDGE,"E12.3.1"),sQuery(id+"F8.wireOp",EDGE,"E12.4.0"),sQuery(id+"F8.wireOp",EDGE,"E12.4.1"),sQuery(id+"F8.wireOp",EDGE,"E12.5.0"),sQuery(id+"F8.wireOp",EDGE,"E12.5.1"),sQuery(id+"F8.wireOp",EDGE,"E12.6.0"),sQuery(id+"F8.wireOp",EDGE,"E13"),sQuery(id+"F8.wireOp",EDGE,"E14")])]}),"instanceName":"1"}),"instanceName":"1"});
            var Q4;
            Q4=sQuery(id+"F25.wireOp",EDGE,"E27");
            circularPattern(context, id + "F26", {"entities" : qUnion([Q0, Q1, Q2, Q3]), "axis" : qUnion([Q4]), "angle" : 72 * degree, "instanceCount" : round(3), "oppositeDirection" : true});
        }
        {
            var Q0;
            Q0=makeQuery(id+"F17.opPattern","COPY",FACE,{"derivedFrom":makeQuery(id+"F3.opExtrude","CAP_FACE",FACE,{"disambiguationData":[OSD([sQuery(id+"F1.wireOp",EDGE,"E2.0"),sQuery(id+"F1.wireOp",EDGE,"E2.1"),sQuery(id+"F1.wireOp",EDGE,"E2.2"),sQuery(id+"F1.wireOp",EDGE,"E2.3"),sQuery(id+"F1.wireOp",EDGE,"E2.4"),sQuery(id+"F1.wireOp",EDGE,"E2.5")])],"isStart":true}),"instanceName":"1"});
            var sketch = newSketch(context, id + "F27", { "sketchPlane" : qUnion([Q0])});
            skLineSegment(sketch, "E28", {"start": v(0, -47.28) * mm, "end": v(0, -21.3) * mm});
            skSolve(sketch);
        }
        {
            var Q0;
            Q0=qCreatedBy(makeId("Right.planeOp"),FACE);
            var sketch = newSketch(context, id + "F28", { "sketchPlane" : qUnion([Q0])});
            skLineSegment(sketch, "E29.0", {"start": v(-35.84, -41.3) * mm, "end": v(-30.97, -15.77) * mm});
            skLineSegment(sketch, "E30", {"start": v(-33.4, -28.53) * mm, "end": v(-47.6, -25.82) * mm});
            skSolve(sketch);
        }
        {
            var Q0;
            Q0=makeQuery(id+"F18.opPattern","COPY",BODY,{"derivedFrom":makeQuery(id+"F2.opExtrude","SWEPT_BODY",BODY,{"disambiguationData":[OSD([sQuery(id+"F0.wireOp",EDGE,"E0.0"),sQuery(id+"F0.wireOp",EDGE,"E0.1"),sQuery(id+"F0.wireOp",EDGE,"E0.2"),sQuery(id+"F0.wireOp",EDGE,"E0.3"),sQuery(id+"F0.wireOp",EDGE,"E0.4")])]}),"instanceName":"2"});
            var Q1;
            Q1=sQuery(id+"F28.wireOp",EDGE,"E30");
            circularPattern(context, id + "F29", {"entities" : qUnion([Q0]), "axis" : qUnion([Q1]), "angle" : 120 * degree, "instanceCount" : 2, "oppositeDirection" : true});
        }
        {
            var Q0;
            Q0=makeQuery(id+"F29.opPattern","COPY",FACE,{"derivedFrom":makeQuery(id+"F18.opPattern","COPY",FACE,{"derivedFrom":makeQuery(id+"F2.opExtrude","CAP_FACE",FACE,{"disambiguationData":[OSD([sQuery(id+"F0.wireOp",EDGE,"E0.0"),sQuery(id+"F0.wireOp",EDGE,"E0.1"),sQuery(id+"F0.wireOp",EDGE,"E0.2"),sQuery(id+"F0.wireOp",EDGE,"E0.3"),sQuery(id+"F0.wireOp",EDGE,"E0.4")])],"isStart":true}),"instanceName":"2"}),"instanceName":"1"});
            var sketch = newSketch(context, id + "F30", { "sketchPlane" : qUnion([Q0])});
            skLineSegment(sketch, "E31", {"start": v(0, -43.99) * mm, "end": v(0, -31.23) * mm});
            skLineSegment(sketch, "E32", {"start": v(-12.14, -35.17) * mm, "end": v(9.82, -28.04) * mm});
            skPoint(sketch, "E33.orphan", {"position": v(0, -20.9) * mm});
            skSolve(sketch);
        }
        {
            var Q0;
            Q0=qCreatedBy(makeId("Right.planeOp"),FACE);
            var sketch = newSketch(context, id + "F31", { "sketchPlane" : qUnion([Q0])});
            skLineSegment(sketch, "E34.0", {"start": v(-25.52, -61.94) * mm, "end": v(-31.23, -50.52) * mm});
            skLineSegment(sketch, "E35", {"start": v(-31.23, -50.52) * mm, "end": v(-51.07, -60.45) * mm});
            skSolve(sketch);
        }
        {
            var Q0;
            Q0=makeQuery(id+"F26.opPattern","COPY",BODY,{"derivedFrom":makeQuery(id+"F3.opExtrude","SWEPT_BODY",BODY,{"disambiguationData":[OSD([sQuery(id+"F1.wireOp",EDGE,"E2.0"),sQuery(id+"F1.wireOp",EDGE,"E2.1"),sQuery(id+"F1.wireOp",EDGE,"E2.2"),sQuery(id+"F1.wireOp",EDGE,"E2.3"),sQuery(id+"F1.wireOp",EDGE,"E2.4"),sQuery(id+"F1.wireOp",EDGE,"E2.5")])]}),"instanceName":"2"});
            var Q1;
            Q1=makeQuery(id+"F26.opPattern","COPY",BODY,{"derivedFrom":makeQuery(id+"F16.opPattern","COPY",BODY,{"derivedFrom":makeQuery(id+"F15.opPattern","COPY",BODY,{"derivedFrom":makeQuery(id+"F9.opExtrude","SWEPT_BODY",BODY,{"disambiguationData":[OSD([sQuery(id+"F8.wireOp",EDGE,"E7.0"),sQuery(id+"F8.wireOp",EDGE,"E10"),sQuery(id+"F8.wireOp",EDGE,"E11"),sQuery(id+"F8.wireOp",EDGE,"E12.1.0"),sQuery(id+"F8.wireOp",EDGE,"E12.1.1"),sQuery(id+"F8.wireOp",EDGE,"E12.2.0"),sQuery(id+"F8.wireOp",EDGE,"E12.2.1"),sQuery(id+"F8.wireOp",EDGE,"E12.3.0"),sQuery(id+"F8.wireOp",EDGE,"E12.3.1"),sQuery(id+"F8.wireOp",EDGE,"E12.4.0"),sQuery(id+"F8.wireOp",EDGE,"E12.4.1"),sQuery(id+"F8.wireOp",EDGE,"E12.5.0"),sQuery(id+"F8.wireOp",EDGE,"E12.5.1"),sQuery(id+"F8.wireOp",EDGE,"E12.6.0"),sQuery(id+"F8.wireOp",EDGE,"E13"),sQuery(id+"F8.wireOp",EDGE,"E14")])]}),"instanceName":"2"}),"instanceName":"1"}),"instanceName":"2"});
            var Q2;
            Q2=makeQuery(id+"F26.opPattern","COPY",BODY,{"derivedFrom":makeQuery(id+"F13.opPattern","COPY",BODY,{"derivedFrom":makeQuery(id+"F9.opExtrude","SWEPT_BODY",BODY,{"disambiguationData":[OSD([sQuery(id+"F8.wireOp",EDGE,"E7.0"),sQuery(id+"F8.wireOp",EDGE,"E10"),sQuery(id+"F8.wireOp",EDGE,"E11"),sQuery(id+"F8.wireOp",EDGE,"E12.1.0"),sQuery(id+"F8.wireOp",EDGE,"E12.1.1"),sQuery(id+"F8.wireOp",EDGE,"E12.2.0"),sQuery(id+"F8.wireOp",EDGE,"E12.2.1"),sQuery(id+"F8.wireOp",EDGE,"E12.3.0"),sQuery(id+"F8.wireOp",EDGE,"E12.3.1"),sQuery(id+"F8.wireOp",EDGE,"E12.4.0"),sQuery(id+"F8.wireOp",EDGE,"E12.4.1"),sQuery(id+"F8.wireOp",EDGE,"E12.5.0"),sQuery(id+"F8.wireOp",EDGE,"E12.5.1"),sQuery(id+"F8.wireOp",EDGE,"E12.6.0"),sQuery(id+"F8.wireOp",EDGE,"E13"),sQuery(id+"F8.wireOp",EDGE,"E14")])]}),"instanceName":"1"}),"instanceName":"2"});
            var Q3;
            Q3=makeQuery(id+"F18.opPattern","COPY",BODY,{"derivedFrom":makeQuery(id+"F13.opPattern","COPY",BODY,{"derivedFrom":makeQuery(id+"F9.opExtrude","SWEPT_BODY",BODY,{"disambiguationData":[OSD([sQuery(id+"F8.wireOp",EDGE,"E7.0"),sQuery(id+"F8.wireOp",EDGE,"E10"),sQuery(id+"F8.wireOp",EDGE,"E11"),sQuery(id+"F8.wireOp",EDGE,"E12.1.0"),sQuery(id+"F8.wireOp",EDGE,"E12.1.1"),sQuery(id+"F8.wireOp",EDGE,"E12.2.0"),sQuery(id+"F8.wireOp",EDGE,"E12.2.1"),sQuery(id+"F8.wireOp",EDGE,"E12.3.0"),sQuery(id+"F8.wireOp",EDGE,"E12.3.1"),sQuery(id+"F8.wireOp",EDGE,"E12.4.0"),sQuery(id+"F8.wireOp",EDGE,"E12.4.1"),sQuery(id+"F8.wireOp",EDGE,"E12.5.0"),sQuery(id+"F8.wireOp",EDGE,"E12.5.1"),sQuery(id+"F8.wireOp",EDGE,"E12.6.0"),sQuery(id+"F8.wireOp",EDGE,"E13"),sQuery(id+"F8.wireOp",EDGE,"E14")])]}),"instanceName":"2"}),"instanceName":"2"});
            var Q4;
            Q4=sQuery(id+"F31.wireOp",EDGE,"E35");
            circularPattern(context, id + "F32", {"entities" : qUnion([Q0, Q1, Q2, Q3]), "axis" : qUnion([Q4]), "angle" : 72 * degree, "instanceCount" : round(3), "oppositeDirection" : true});
        }
        {
            var Q0;
            Q0=makeQuery(id+"F6.opPattern","COPY",FACE,{"derivedFrom":makeQuery(id+"F3.opExtrude","CAP_FACE",FACE,{"disambiguationData":[OSD([sQuery(id+"F1.wireOp",EDGE,"E2.0"),sQuery(id+"F1.wireOp",EDGE,"E2.1"),sQuery(id+"F1.wireOp",EDGE,"E2.2"),sQuery(id+"F1.wireOp",EDGE,"E2.3"),sQuery(id+"F1.wireOp",EDGE,"E2.4"),sQuery(id+"F1.wireOp",EDGE,"E2.5")])],"isStart":true}),"instanceName":"2"});
            var sketch = newSketch(context, id + "F33", { "sketchPlane" : qUnion([Q0])});
            skLineSegment(sketch, "E36", {"start": v(-4.1, 7.1) * mm, "end": v(-17.1, 29.6) * mm});
            skSolve(sketch);
        }
        {
            var Q0;
            Q0=sQuery(id+"F33.wireOp",VERTEX,"E36.end");
            var Q1;
            Q1=sQuery(id+"F33.wireOp",VERTEX,"E36.start");
            var Q2;
            Q2=sQuery(id+"F11.wireOp",VERTEX,"E16.end");
            cPlane(context, id + "F34", {"entities" : qUnion([Q0, Q1, Q2]), "cplaneType" : CPlaneType.THREE_POINT, "offset" : 150 * mm, "width" : 150 * mm, "height" : 150 * mm});
        }
        {
            var Q0;
            Q0=qCreatedBy(id+"F34.planeOp",FACE);
            var sketch = newSketch(context, id + "F35", { "sketchPlane" : qUnion([Q0])});
            skLineSegment(sketch, "E37.0", {"start": v(10.32, 0) * mm, "end": v(30.97, -15.77) * mm});
            skLineSegment(sketch, "E38", {"start": v(20.65, -7.89) * mm, "end": v(38.57, 15.58) * mm});
            skSolve(sketch);
        }
        {
            var Q0;
            Q0=makeQuery(id+"F2.opExtrude","SWEPT_BODY",BODY,{"disambiguationData":[OSD([sQuery(id+"F0.wireOp",EDGE,"E0.0"),sQuery(id+"F0.wireOp",EDGE,"E0.1"),sQuery(id+"F0.wireOp",EDGE,"E0.2"),sQuery(id+"F0.wireOp",EDGE,"E0.3"),sQuery(id+"F0.wireOp",EDGE,"E0.4")])]});
            var Q1;
            Q1=sQuery(id+"F35.wireOp",EDGE,"E38");
            circularPattern(context, id + "F36", {"entities" : qUnion([Q0]), "axis" : qUnion([Q1]), "angle" : 120 * degree, "instanceCount" : round(3), "oppositeDirection" : true});
        }
        {
            var Q0;
            Q0=makeQuery(id+"F36.opPattern","COPY",FACE,{"derivedFrom":makeQuery(id+"F2.opExtrude","CAP_FACE",FACE,{"disambiguationData":[OSD([sQuery(id+"F0.wireOp",EDGE,"E0.0"),sQuery(id+"F0.wireOp",EDGE,"E0.1"),sQuery(id+"F0.wireOp",EDGE,"E0.2"),sQuery(id+"F0.wireOp",EDGE,"E0.3"),sQuery(id+"F0.wireOp",EDGE,"E0.4")])],"isStart":true}),"instanceName":"1"});
            var sketch = newSketch(context, id + "F37", { "sketchPlane" : qUnion([Q0])});
            skLineSegment(sketch, "E39", {"start": v(-4.5, -30.9) * mm, "end": v(1.45, -42.2) * mm});
            skPoint(sketch, "E40.orphan", {"position": v(-9.3, -21.76) * mm});
            skSolve(sketch);
        }
        {
            var Q0;
            Q0=sQuery(id+"F37.wireOp",VERTEX,"E39.end");
            var Q1;
            Q1=sQuery(id+"F37.wireOp",VERTEX,"E39.start");
            var Q2;
            Q2=sQuery(id+"F35.wireOp",VERTEX,"E38.end");
            cPlane(context, id + "F38", {"entities" : qUnion([Q0, Q1, Q2]), "cplaneType" : CPlaneType.THREE_POINT, "offset" : 150 * mm, "width" : 150 * mm, "height" : 150 * mm});
        }
        {
            var Q0;
            Q0=qCreatedBy(id+"F38.planeOp",FACE);
            var sketch = newSketch(context, id + "F39", { "sketchPlane" : qUnion([Q0])});
            skLineSegment(sketch, "E41.0", {"start": v(29.7, -11.34) * mm, "end": v(36.4, -22.2) * mm});
            skLineSegment(sketch, "E42", {"start": v(29.7, -11.34) * mm, "end": v(58.3, 6.33) * mm});
            skSolve(sketch);
        }
        {
            var Q0;
            Q0=makeQuery(id+"F22.opPattern","COPY",BODY,{"derivedFrom":makeQuery(id+"F17.opPattern","COPY",BODY,{"derivedFrom":makeQuery(id+"F3.opExtrude","SWEPT_BODY",BODY,{"disambiguationData":[OSD([sQuery(id+"F1.wireOp",EDGE,"E2.0"),sQuery(id+"F1.wireOp",EDGE,"E2.1"),sQuery(id+"F1.wireOp",EDGE,"E2.2"),sQuery(id+"F1.wireOp",EDGE,"E2.3"),sQuery(id+"F1.wireOp",EDGE,"E2.4"),sQuery(id+"F1.wireOp",EDGE,"E2.5")])]}),"instanceName":"1"}),"instanceName":"2"});
            var Q1;
            Q1=makeQuery(id+"F22.opPattern","COPY",BODY,{"derivedFrom":makeQuery(id+"F17.opPattern","COPY",BODY,{"derivedFrom":makeQuery(id+"F16.opPattern","COPY",BODY,{"derivedFrom":makeQuery(id+"F15.opPattern","COPY",BODY,{"derivedFrom":makeQuery(id+"F9.opExtrude","SWEPT_BODY",BODY,{"disambiguationData":[OSD([sQuery(id+"F8.wireOp",EDGE,"E7.0"),sQuery(id+"F8.wireOp",EDGE,"E10"),sQuery(id+"F8.wireOp",EDGE,"E11"),sQuery(id+"F8.wireOp",EDGE,"E12.1.0"),sQuery(id+"F8.wireOp",EDGE,"E12.1.1"),sQuery(id+"F8.wireOp",EDGE,"E12.2.0"),sQuery(id+"F8.wireOp",EDGE,"E12.2.1"),sQuery(id+"F8.wireOp",EDGE,"E12.3.0"),sQuery(id+"F8.wireOp",EDGE,"E12.3.1"),sQuery(id+"F8.wireOp",EDGE,"E12.4.0"),sQuery(id+"F8.wireOp",EDGE,"E12.4.1"),sQuery(id+"F8.wireOp",EDGE,"E12.5.0"),sQuery(id+"F8.wireOp",EDGE,"E12.5.1"),sQuery(id+"F8.wireOp",EDGE,"E12.6.0"),sQuery(id+"F8.wireOp",EDGE,"E13"),sQuery(id+"F8.wireOp",EDGE,"E14")])]}),"instanceName":"2"}),"instanceName":"1"}),"instanceName":"1"}),"instanceName":"2"});
            var Q2;
            Q2=makeQuery(id+"F22.opPattern","COPY",BODY,{"derivedFrom":makeQuery(id+"F17.opPattern","COPY",BODY,{"derivedFrom":makeQuery(id+"F13.opPattern","COPY",BODY,{"derivedFrom":makeQuery(id+"F9.opExtrude","SWEPT_BODY",BODY,{"disambiguationData":[OSD([sQuery(id+"F8.wireOp",EDGE,"E7.0"),sQuery(id+"F8.wireOp",EDGE,"E10"),sQuery(id+"F8.wireOp",EDGE,"E11"),sQuery(id+"F8.wireOp",EDGE,"E12.1.0"),sQuery(id+"F8.wireOp",EDGE,"E12.1.1"),sQuery(id+"F8.wireOp",EDGE,"E12.2.0"),sQuery(id+"F8.wireOp",EDGE,"E12.2.1"),sQuery(id+"F8.wireOp",EDGE,"E12.3.0"),sQuery(id+"F8.wireOp",EDGE,"E12.3.1"),sQuery(id+"F8.wireOp",EDGE,"E12.4.0"),sQuery(id+"F8.wireOp",EDGE,"E12.4.1"),sQuery(id+"F8.wireOp",EDGE,"E12.5.0"),sQuery(id+"F8.wireOp",EDGE,"E12.5.1"),sQuery(id+"F8.wireOp",EDGE,"E12.6.0"),sQuery(id+"F8.wireOp",EDGE,"E13"),sQuery(id+"F8.wireOp",EDGE,"E14")])]}),"instanceName":"1"}),"instanceName":"1"}),"instanceName":"2"});
            var Q3;
            Q3=makeQuery(id+"F18.opPattern","COPY",BODY,{"derivedFrom":makeQuery(id+"F13.opPattern","COPY",BODY,{"derivedFrom":makeQuery(id+"F9.opExtrude","SWEPT_BODY",BODY,{"disambiguationData":[OSD([sQuery(id+"F8.wireOp",EDGE,"E7.0"),sQuery(id+"F8.wireOp",EDGE,"E10"),sQuery(id+"F8.wireOp",EDGE,"E11"),sQuery(id+"F8.wireOp",EDGE,"E12.1.0"),sQuery(id+"F8.wireOp",EDGE,"E12.1.1"),sQuery(id+"F8.wireOp",EDGE,"E12.2.0"),sQuery(id+"F8.wireOp",EDGE,"E12.2.1"),sQuery(id+"F8.wireOp",EDGE,"E12.3.0"),sQuery(id+"F8.wireOp",EDGE,"E12.3.1"),sQuery(id+"F8.wireOp",EDGE,"E12.4.0"),sQuery(id+"F8.wireOp",EDGE,"E12.4.1"),sQuery(id+"F8.wireOp",EDGE,"E12.5.0"),sQuery(id+"F8.wireOp",EDGE,"E12.5.1"),sQuery(id+"F8.wireOp",EDGE,"E12.6.0"),sQuery(id+"F8.wireOp",EDGE,"E13"),sQuery(id+"F8.wireOp",EDGE,"E14")])]}),"instanceName":"2"}),"instanceName":"1"});
            var Q4;
            Q4=sQuery(id+"F39.wireOp",EDGE,"E42");
            circularPattern(context, id + "F40", {"entities" : qUnion([Q0, Q1, Q2, Q3]), "axis" : qUnion([Q4]), "angle" : 72 * degree, "instanceCount" : round(3), "oppositeDirection" : true});
        }
        {
            var Q0;
            Q0=makeQuery(id+"F36.opPattern","COPY",FACE,{"derivedFrom":makeQuery(id+"F2.opExtrude","CAP_FACE",FACE,{"disambiguationData":[OSD([sQuery(id+"F0.wireOp",EDGE,"E0.0"),sQuery(id+"F0.wireOp",EDGE,"E0.1"),sQuery(id+"F0.wireOp",EDGE,"E0.2"),sQuery(id+"F0.wireOp",EDGE,"E0.3"),sQuery(id+"F0.wireOp",EDGE,"E0.4")])],"isStart":true}),"instanceName":"2"});
            var sketch = newSketch(context, id + "F41", { "sketchPlane" : qUnion([Q0])});
            skLineSegment(sketch, "E43", {"start": v(0, -18.47) * mm, "end": v(0, -31.23) * mm});
            skPoint(sketch, "E44.orphan", {"position": v(0, -41.55) * mm});
            skSolve(sketch);
        }
        {
            var Q0;
            Q0=sQuery(id+"F41.wireOp",VERTEX,"E43.end");
            var Q1;
            Q1=sQuery(id+"F41.wireOp",VERTEX,"E43.start");
            var Q2;
            Q2=sQuery(id+"F11.wireOp",VERTEX,"E16.end");
            cPlane(context, id + "F42", {"entities" : qUnion([Q0, Q1, Q2]), "cplaneType" : CPlaneType.THREE_POINT, "offset" : 150 * mm, "width" : 150 * mm, "height" : 150 * mm});
        }
        {
            var Q0;
            Q0=qCreatedBy(id+"F42.planeOp",FACE);
            var sketch = newSketch(context, id + "F43", { "sketchPlane" : qUnion([Q0])});
            skLineSegment(sketch, "E45.0", {"start": v(-25.52, -7.89) * mm, "end": v(-31.23, -19.3) * mm});
            skLineSegment(sketch, "E46", {"start": v(-31.23, -19.3) * mm, "end": v(-78.41, 4.3) * mm});
            skSolve(sketch);
        }
        {
            var Q0;
            Q0=makeQuery(id+"F40.opPattern","COPY",BODY,{"derivedFrom":makeQuery(id+"F22.opPattern","COPY",BODY,{"derivedFrom":makeQuery(id+"F17.opPattern","COPY",BODY,{"derivedFrom":makeQuery(id+"F3.opExtrude","SWEPT_BODY",BODY,{"disambiguationData":[OSD([sQuery(id+"F1.wireOp",EDGE,"E2.0"),sQuery(id+"F1.wireOp",EDGE,"E2.1"),sQuery(id+"F1.wireOp",EDGE,"E2.2"),sQuery(id+"F1.wireOp",EDGE,"E2.3"),sQuery(id+"F1.wireOp",EDGE,"E2.4"),sQuery(id+"F1.wireOp",EDGE,"E2.5")])]}),"instanceName":"1"}),"instanceName":"2"}),"instanceName":"2"});
            var Q1;
            Q1=makeQuery(id+"F40.opPattern","COPY",BODY,{"derivedFrom":makeQuery(id+"F22.opPattern","COPY",BODY,{"derivedFrom":makeQuery(id+"F17.opPattern","COPY",BODY,{"derivedFrom":makeQuery(id+"F13.opPattern","COPY",BODY,{"derivedFrom":makeQuery(id+"F9.opExtrude","SWEPT_BODY",BODY,{"disambiguationData":[OSD([sQuery(id+"F8.wireOp",EDGE,"E7.0"),sQuery(id+"F8.wireOp",EDGE,"E10"),sQuery(id+"F8.wireOp",EDGE,"E11"),sQuery(id+"F8.wireOp",EDGE,"E12.1.0"),sQuery(id+"F8.wireOp",EDGE,"E12.1.1"),sQuery(id+"F8.wireOp",EDGE,"E12.2.0"),sQuery(id+"F8.wireOp",EDGE,"E12.2.1"),sQuery(id+"F8.wireOp",EDGE,"E12.3.0"),sQuery(id+"F8.wireOp",EDGE,"E12.3.1"),sQuery(id+"F8.wireOp",EDGE,"E12.4.0"),sQuery(id+"F8.wireOp",EDGE,"E12.4.1"),sQuery(id+"F8.wireOp",EDGE,"E12.5.0"),sQuery(id+"F8.wireOp",EDGE,"E12.5.1"),sQuery(id+"F8.wireOp",EDGE,"E12.6.0"),sQuery(id+"F8.wireOp",EDGE,"E13"),sQuery(id+"F8.wireOp",EDGE,"E14")])]}),"instanceName":"1"}),"instanceName":"1"}),"instanceName":"2"}),"instanceName":"2"});
            var Q2;
            Q2=makeQuery(id+"F40.opPattern","COPY",BODY,{"derivedFrom":makeQuery(id+"F18.opPattern","COPY",BODY,{"derivedFrom":makeQuery(id+"F13.opPattern","COPY",BODY,{"derivedFrom":makeQuery(id+"F9.opExtrude","SWEPT_BODY",BODY,{"disambiguationData":[OSD([sQuery(id+"F8.wireOp",EDGE,"E7.0"),sQuery(id+"F8.wireOp",EDGE,"E10"),sQuery(id+"F8.wireOp",EDGE,"E11"),sQuery(id+"F8.wireOp",EDGE,"E12.1.0"),sQuery(id+"F8.wireOp",EDGE,"E12.1.1"),sQuery(id+"F8.wireOp",EDGE,"E12.2.0"),sQuery(id+"F8.wireOp",EDGE,"E12.2.1"),sQuery(id+"F8.wireOp",EDGE,"E12.3.0"),sQuery(id+"F8.wireOp",EDGE,"E12.3.1"),sQuery(id+"F8.wireOp",EDGE,"E12.4.0"),sQuery(id+"F8.wireOp",EDGE,"E12.4.1"),sQuery(id+"F8.wireOp",EDGE,"E12.5.0"),sQuery(id+"F8.wireOp",EDGE,"E12.5.1"),sQuery(id+"F8.wireOp",EDGE,"E12.6.0"),sQuery(id+"F8.wireOp",EDGE,"E13"),sQuery(id+"F8.wireOp",EDGE,"E14")])]}),"instanceName":"2"}),"instanceName":"1"}),"instanceName":"2"});
            var Q3;
            Q3=makeQuery(id+"F40.opPattern","COPY",BODY,{"derivedFrom":makeQuery(id+"F22.opPattern","COPY",BODY,{"derivedFrom":makeQuery(id+"F17.opPattern","COPY",BODY,{"derivedFrom":makeQuery(id+"F16.opPattern","COPY",BODY,{"derivedFrom":makeQuery(id+"F15.opPattern","COPY",BODY,{"derivedFrom":makeQuery(id+"F9.opExtrude","SWEPT_BODY",BODY,{"disambiguationData":[OSD([sQuery(id+"F8.wireOp",EDGE,"E7.0"),sQuery(id+"F8.wireOp",EDGE,"E10"),sQuery(id+"F8.wireOp",EDGE,"E11"),sQuery(id+"F8.wireOp",EDGE,"E12.1.0"),sQuery(id+"F8.wireOp",EDGE,"E12.1.1"),sQuery(id+"F8.wireOp",EDGE,"E12.2.0"),sQuery(id+"F8.wireOp",EDGE,"E12.2.1"),sQuery(id+"F8.wireOp",EDGE,"E12.3.0"),sQuery(id+"F8.wireOp",EDGE,"E12.3.1"),sQuery(id+"F8.wireOp",EDGE,"E12.4.0"),sQuery(id+"F8.wireOp",EDGE,"E12.4.1"),sQuery(id+"F8.wireOp",EDGE,"E12.5.0"),sQuery(id+"F8.wireOp",EDGE,"E12.5.1"),sQuery(id+"F8.wireOp",EDGE,"E12.6.0"),sQuery(id+"F8.wireOp",EDGE,"E13"),sQuery(id+"F8.wireOp",EDGE,"E14")])]}),"instanceName":"2"}),"instanceName":"1"}),"instanceName":"1"}),"instanceName":"2"}),"instanceName":"2"});
            var Q4;
            Q4=sQuery(id+"F43.wireOp",EDGE,"E46");
            circularPattern(context, id + "F44", {"entities" : qUnion([Q0, Q1, Q2, Q3]), "axis" : qUnion([Q4]), "angle" : 72 * degree, "instanceCount" : round(3), "oppositeDirection" : true});
        }
        {
            var Q0;
            Q0=makeQuery(id+"F40.opPattern","COPY",FACE,{"derivedFrom":makeQuery(id+"F22.opPattern","COPY",FACE,{"derivedFrom":makeQuery(id+"F17.opPattern","COPY",FACE,{"derivedFrom":makeQuery(id+"F3.opExtrude","CAP_FACE",FACE,{"disambiguationData":[OSD([sQuery(id+"F1.wireOp",EDGE,"E2.0"),sQuery(id+"F1.wireOp",EDGE,"E2.1"),sQuery(id+"F1.wireOp",EDGE,"E2.2"),sQuery(id+"F1.wireOp",EDGE,"E2.3"),sQuery(id+"F1.wireOp",EDGE,"E2.4"),sQuery(id+"F1.wireOp",EDGE,"E2.5")])],"isStart":true}),"instanceName":"1"}),"instanceName":"2"}),"instanceName":"1"});
            var sketch = newSketch(context, id + "F45", { "sketchPlane" : qUnion([Q0])});
            skLineSegment(sketch, "E47", {"start": v(1.3, -21.26) * mm, "end": v(2.09, -34.23) * mm});
            skSolve(sketch);
        }
        {
            var Q0;
            Q0=sQuery(id+"F45.wireOp",VERTEX,"E47.end");
            var Q1;
            Q1=sQuery(id+"F45.wireOp",VERTEX,"E47.start");
            var Q2;
            Q2=makeQuery(id+"F6.opPattern","COPY",VERTEX,{"derivedFrom":makeQuery(id+"F3.opExtrude","CAP_VERTEX",VERTEX,{"disambiguationData":[OSD([sQuery(id+"F1.wireOp",EDGE,"E2.1"),sQuery(id+"F1.wireOp",EDGE,"E2.2")])],"isStart":true}),"instanceName":"3"});
            cPlane(context, id + "F46", {"entities" : qUnion([Q0, Q1, Q2]), "cplaneType" : CPlaneType.THREE_POINT, "offset" : 150 * mm, "width" : 150 * mm, "height" : 150 * mm});
        }
        {
            var Q0;
            Q0=qCreatedBy(id+"F46.planeOp",FACE);
            var sketch = newSketch(context, id + "F47", { "sketchPlane" : qUnion([Q0])});
            skLineSegment(sketch, "E48.0", {"start": v(-35.84, -28.53) * mm, "end": v(-33.4, -41.3) * mm});
            skLineSegment(sketch, "E49", {"start": v(-33.4, -41.3) * mm, "end": v(-61.9, -46.73) * mm});
            skSolve(sketch);
        }
        {
            var Q0;
            Q0=makeQuery(id+"F22.opPattern","COPY",BODY,{"derivedFrom":makeQuery(id+"F17.opPattern","COPY",BODY,{"derivedFrom":makeQuery(id+"F3.opExtrude","SWEPT_BODY",BODY,{"disambiguationData":[OSD([sQuery(id+"F1.wireOp",EDGE,"E2.0"),sQuery(id+"F1.wireOp",EDGE,"E2.1"),sQuery(id+"F1.wireOp",EDGE,"E2.2"),sQuery(id+"F1.wireOp",EDGE,"E2.3"),sQuery(id+"F1.wireOp",EDGE,"E2.4"),sQuery(id+"F1.wireOp",EDGE,"E2.5")])]}),"instanceName":"1"}),"instanceName":"2"});
            var Q1;
            Q1=makeQuery(id+"F22.opPattern","COPY",BODY,{"derivedFrom":makeQuery(id+"F17.opPattern","COPY",BODY,{"derivedFrom":makeQuery(id+"F13.opPattern","COPY",BODY,{"derivedFrom":makeQuery(id+"F9.opExtrude","SWEPT_BODY",BODY,{"disambiguationData":[OSD([sQuery(id+"F8.wireOp",EDGE,"E7.0"),sQuery(id+"F8.wireOp",EDGE,"E10"),sQuery(id+"F8.wireOp",EDGE,"E11"),sQuery(id+"F8.wireOp",EDGE,"E12.1.0"),sQuery(id+"F8.wireOp",EDGE,"E12.1.1"),sQuery(id+"F8.wireOp",EDGE,"E12.2.0"),sQuery(id+"F8.wireOp",EDGE,"E12.2.1"),sQuery(id+"F8.wireOp",EDGE,"E12.3.0"),sQuery(id+"F8.wireOp",EDGE,"E12.3.1"),sQuery(id+"F8.wireOp",EDGE,"E12.4.0"),sQuery(id+"F8.wireOp",EDGE,"E12.4.1"),sQuery(id+"F8.wireOp",EDGE,"E12.5.0"),sQuery(id+"F8.wireOp",EDGE,"E12.5.1"),sQuery(id+"F8.wireOp",EDGE,"E12.6.0"),sQuery(id+"F8.wireOp",EDGE,"E13"),sQuery(id+"F8.wireOp",EDGE,"E14")])]}),"instanceName":"1"}),"instanceName":"1"}),"instanceName":"2"});
            var Q2;
            Q2=makeQuery(id+"F22.opPattern","COPY",BODY,{"derivedFrom":makeQuery(id+"F17.opPattern","COPY",BODY,{"derivedFrom":makeQuery(id+"F16.opPattern","COPY",BODY,{"derivedFrom":makeQuery(id+"F15.opPattern","COPY",BODY,{"derivedFrom":makeQuery(id+"F9.opExtrude","SWEPT_BODY",BODY,{"disambiguationData":[OSD([sQuery(id+"F8.wireOp",EDGE,"E7.0"),sQuery(id+"F8.wireOp",EDGE,"E10"),sQuery(id+"F8.wireOp",EDGE,"E11"),sQuery(id+"F8.wireOp",EDGE,"E12.1.0"),sQuery(id+"F8.wireOp",EDGE,"E12.1.1"),sQuery(id+"F8.wireOp",EDGE,"E12.2.0"),sQuery(id+"F8.wireOp",EDGE,"E12.2.1"),sQuery(id+"F8.wireOp",EDGE,"E12.3.0"),sQuery(id+"F8.wireOp",EDGE,"E12.3.1"),sQuery(id+"F8.wireOp",EDGE,"E12.4.0"),sQuery(id+"F8.wireOp",EDGE,"E12.4.1"),sQuery(id+"F8.wireOp",EDGE,"E12.5.0"),sQuery(id+"F8.wireOp",EDGE,"E12.5.1"),sQuery(id+"F8.wireOp",EDGE,"E12.6.0"),sQuery(id+"F8.wireOp",EDGE,"E13"),sQuery(id+"F8.wireOp",EDGE,"E14")])]}),"instanceName":"2"}),"instanceName":"1"}),"instanceName":"1"}),"instanceName":"2"});
            var Q3;
            Q3=makeQuery(id+"F18.opPattern","COPY",BODY,{"derivedFrom":makeQuery(id+"F13.opPattern","COPY",BODY,{"derivedFrom":makeQuery(id+"F9.opExtrude","SWEPT_BODY",BODY,{"disambiguationData":[OSD([sQuery(id+"F8.wireOp",EDGE,"E7.0"),sQuery(id+"F8.wireOp",EDGE,"E10"),sQuery(id+"F8.wireOp",EDGE,"E11"),sQuery(id+"F8.wireOp",EDGE,"E12.1.0"),sQuery(id+"F8.wireOp",EDGE,"E12.1.1"),sQuery(id+"F8.wireOp",EDGE,"E12.2.0"),sQuery(id+"F8.wireOp",EDGE,"E12.2.1"),sQuery(id+"F8.wireOp",EDGE,"E12.3.0"),sQuery(id+"F8.wireOp",EDGE,"E12.3.1"),sQuery(id+"F8.wireOp",EDGE,"E12.4.0"),sQuery(id+"F8.wireOp",EDGE,"E12.4.1"),sQuery(id+"F8.wireOp",EDGE,"E12.5.0"),sQuery(id+"F8.wireOp",EDGE,"E12.5.1"),sQuery(id+"F8.wireOp",EDGE,"E12.6.0"),sQuery(id+"F8.wireOp",EDGE,"E13"),sQuery(id+"F8.wireOp",EDGE,"E14")])]}),"instanceName":"2"}),"instanceName":"1"});
            var Q4;
            Q4=sQuery(id+"F47.wireOp",EDGE,"E49");
            circularPattern(context, id + "F48", {"entities" : qUnion([Q0, Q1, Q2, Q3]), "axis" : qUnion([Q4]), "angle" : 120 * degree, "instanceCount" : 2, "oppositeDirection" : true});
        }
        {
            var Q0;
            Q0=makeQuery(id+"F26.opPattern","COPY",FACE,{"derivedFrom":makeQuery(id+"F3.opExtrude","CAP_FACE",FACE,{"disambiguationData":[OSD([sQuery(id+"F1.wireOp",EDGE,"E2.0"),sQuery(id+"F1.wireOp",EDGE,"E2.1"),sQuery(id+"F1.wireOp",EDGE,"E2.2"),sQuery(id+"F1.wireOp",EDGE,"E2.3"),sQuery(id+"F1.wireOp",EDGE,"E2.4"),sQuery(id+"F1.wireOp",EDGE,"E2.5")])],"isStart":true}),"instanceName":"1"});
            var sketch = newSketch(context, id + "F49", { "sketchPlane" : qUnion([Q0])});
            skLineSegment(sketch, "E50", {"start": v(-12.92, -27.06) * mm, "end": v(-2.09, -34.23) * mm});
            skSolve(sketch);
        }
        {
            var Q0;
            Q0=sQuery(id+"F49.wireOp",VERTEX,"E50.end");
            var Q1;
            Q1=sQuery(id+"F49.wireOp",VERTEX,"E50.start");
            var Q2;
            Q2=makeQuery(id+"F6.opPattern","COPY",VERTEX,{"derivedFrom":makeQuery(id+"F3.opExtrude","CAP_VERTEX",VERTEX,{"disambiguationData":[OSD([sQuery(id+"F1.wireOp",EDGE,"E2.0"),sQuery(id+"F1.wireOp",EDGE,"E2.5")])],"isStart":true}),"instanceName":"4"});
            cPlane(context, id + "F50", {"entities" : qUnion([Q0, Q1, Q2]), "cplaneType" : CPlaneType.THREE_POINT, "offset" : 150 * mm, "width" : 150 * mm, "height" : 150 * mm});
        }
        {
            var Q0;
            Q0=qCreatedBy(id+"F50.planeOp",FACE);
            var sketch = newSketch(context, id + "F51", { "sketchPlane" : qUnion([Q0])});
            skLineSegment(sketch, "E51.0", {"start": v(27.14, -5.92) * mm, "end": v(31.77, 6.22) * mm});
            skLineSegment(sketch, "E52", {"start": v(31.77, 6.22) * mm, "end": v(70.56, -8.6) * mm});
            skSolve(sketch);
        }
        {
            var Q0;
            Q0=makeQuery(id+"F16.opPattern","COPY",BODY,{"derivedFrom":makeQuery(id+"F15.opPattern","COPY",BODY,{"derivedFrom":makeQuery(id+"F9.opExtrude","SWEPT_BODY",BODY,{"disambiguationData":[OSD([sQuery(id+"F8.wireOp",EDGE,"E7.0"),sQuery(id+"F8.wireOp",EDGE,"E10"),sQuery(id+"F8.wireOp",EDGE,"E11"),sQuery(id+"F8.wireOp",EDGE,"E12.1.0"),sQuery(id+"F8.wireOp",EDGE,"E12.1.1"),sQuery(id+"F8.wireOp",EDGE,"E12.2.0"),sQuery(id+"F8.wireOp",EDGE,"E12.2.1"),sQuery(id+"F8.wireOp",EDGE,"E12.3.0"),sQuery(id+"F8.wireOp",EDGE,"E12.3.1"),sQuery(id+"F8.wireOp",EDGE,"E12.4.0"),sQuery(id+"F8.wireOp",EDGE,"E12.4.1"),sQuery(id+"F8.wireOp",EDGE,"E12.5.0"),sQuery(id+"F8.wireOp",EDGE,"E12.5.1"),sQuery(id+"F8.wireOp",EDGE,"E12.6.0"),sQuery(id+"F8.wireOp",EDGE,"E13"),sQuery(id+"F8.wireOp",EDGE,"E14")])]}),"instanceName":"1"}),"instanceName":"1"});
            var Q1;
            Q1=makeQuery(id+"F13.opPattern","COPY",BODY,{"derivedFrom":makeQuery(id+"F9.opExtrude","SWEPT_BODY",BODY,{"disambiguationData":[OSD([sQuery(id+"F8.wireOp",EDGE,"E7.0"),sQuery(id+"F8.wireOp",EDGE,"E10"),sQuery(id+"F8.wireOp",EDGE,"E11"),sQuery(id+"F8.wireOp",EDGE,"E12.1.0"),sQuery(id+"F8.wireOp",EDGE,"E12.1.1"),sQuery(id+"F8.wireOp",EDGE,"E12.2.0"),sQuery(id+"F8.wireOp",EDGE,"E12.2.1"),sQuery(id+"F8.wireOp",EDGE,"E12.3.0"),sQuery(id+"F8.wireOp",EDGE,"E12.3.1"),sQuery(id+"F8.wireOp",EDGE,"E12.4.0"),sQuery(id+"F8.wireOp",EDGE,"E12.4.1"),sQuery(id+"F8.wireOp",EDGE,"E12.5.0"),sQuery(id+"F8.wireOp",EDGE,"E12.5.1"),sQuery(id+"F8.wireOp",EDGE,"E12.6.0"),sQuery(id+"F8.wireOp",EDGE,"E13"),sQuery(id+"F8.wireOp",EDGE,"E14")])]}),"instanceName":"1"});
            var Q2;
            Q2=makeQuery(id+"F16.opPattern","COPY",BODY,{"derivedFrom":makeQuery(id+"F15.opPattern","COPY",BODY,{"derivedFrom":makeQuery(id+"F9.opExtrude","SWEPT_BODY",BODY,{"disambiguationData":[OSD([sQuery(id+"F8.wireOp",EDGE,"E7.0"),sQuery(id+"F8.wireOp",EDGE,"E10"),sQuery(id+"F8.wireOp",EDGE,"E11"),sQuery(id+"F8.wireOp",EDGE,"E12.1.0"),sQuery(id+"F8.wireOp",EDGE,"E12.1.1"),sQuery(id+"F8.wireOp",EDGE,"E12.2.0"),sQuery(id+"F8.wireOp",EDGE,"E12.2.1"),sQuery(id+"F8.wireOp",EDGE,"E12.3.0"),sQuery(id+"F8.wireOp",EDGE,"E12.3.1"),sQuery(id+"F8.wireOp",EDGE,"E12.4.0"),sQuery(id+"F8.wireOp",EDGE,"E12.4.1"),sQuery(id+"F8.wireOp",EDGE,"E12.5.0"),sQuery(id+"F8.wireOp",EDGE,"E12.5.1"),sQuery(id+"F8.wireOp",EDGE,"E12.6.0"),sQuery(id+"F8.wireOp",EDGE,"E13"),sQuery(id+"F8.wireOp",EDGE,"E14")])]}),"instanceName":"2"}),"instanceName":"1"});
            var Q3;
            Q3=makeQuery(id+"F3.opExtrude","SWEPT_BODY",BODY,{"disambiguationData":[OSD([sQuery(id+"F1.wireOp",EDGE,"E2.0"),sQuery(id+"F1.wireOp",EDGE,"E2.1"),sQuery(id+"F1.wireOp",EDGE,"E2.2"),sQuery(id+"F1.wireOp",EDGE,"E2.3"),sQuery(id+"F1.wireOp",EDGE,"E2.4"),sQuery(id+"F1.wireOp",EDGE,"E2.5")])]});
            var Q4;
            Q4=sQuery(id+"F51.wireOp",EDGE,"E52");
            circularPattern(context, id + "F52", {"entities" : qUnion([Q0, Q1, Q2, Q3]), "axis" : qUnion([Q4]), "angle" : 120 * degree, "instanceCount" : round(2), "oppositeDirection" : true});
        }
        {
            var Q0;
            Q0=makeQuery(id+"F32.opPattern","COPY",FACE,{"derivedFrom":makeQuery(id+"F26.opPattern","COPY",FACE,{"derivedFrom":makeQuery(id+"F3.opExtrude","CAP_FACE",FACE,{"disambiguationData":[OSD([sQuery(id+"F1.wireOp",EDGE,"E2.0"),sQuery(id+"F1.wireOp",EDGE,"E2.1"),sQuery(id+"F1.wireOp",EDGE,"E2.2"),sQuery(id+"F1.wireOp",EDGE,"E2.3"),sQuery(id+"F1.wireOp",EDGE,"E2.4"),sQuery(id+"F1.wireOp",EDGE,"E2.5")])],"isStart":true}),"instanceName":"2"}),"instanceName":"1"});
            var sketch = newSketch(context, id + "F53", { "sketchPlane" : qUnion([Q0])});
            skLineSegment(sketch, "E53", {"start": v(-10.6, -33.35) * mm, "end": v(-10.6, -18.35) * mm});
            skSolve(sketch);
        }
        {
            var Q0;
            Q0=sQuery(id+"F53.wireOp",VERTEX,"E53.start");
            var Q1;
            Q1=sQuery(id+"F53.wireOp",VERTEX,"E53.end");
            var Q2;
            Q2=makeQuery(id+"F32.opPattern","COPY",VERTEX,{"derivedFrom":makeQuery(id+"F26.opPattern","COPY",VERTEX,{"derivedFrom":makeQuery(id+"F3.opExtrude","CAP_VERTEX",VERTEX,{"disambiguationData":[OSD([sQuery(id+"F1.wireOp",EDGE,"E2.2"),sQuery(id+"F1.wireOp",EDGE,"E2.3")])],"isStart":false}),"instanceName":"2"}),"instanceName":"1"});
            cPlane(context, id + "F54", {"entities" : qUnion([Q0, Q1, Q2]), "cplaneType" : CPlaneType.THREE_POINT, "offset" : 150 * mm, "width" : 150 * mm, "height" : 150 * mm});
        }
        {
            var Q0;
            Q0=qCreatedBy(id+"F54.planeOp",FACE);
            var sketch = newSketch(context, id + "F55", { "sketchPlane" : qUnion([Q0])});
            skLineSegment(sketch, "E54.0", {"start": v(-2, -70.16) * mm, "end": v(-14.98, -62.66) * mm});
            skLineSegment(sketch, "E55", {"start": v(-14.98, -62.66) * mm, "end": v(-37.7, -102) * mm});
            skSolve(sketch);
        }
        {
            var Q0;
            Q0=makeQuery(id+"F26.opPattern","COPY",BODY,{"derivedFrom":makeQuery(id+"F3.opExtrude","SWEPT_BODY",BODY,{"disambiguationData":[OSD([sQuery(id+"F1.wireOp",EDGE,"E2.0"),sQuery(id+"F1.wireOp",EDGE,"E2.1"),sQuery(id+"F1.wireOp",EDGE,"E2.2"),sQuery(id+"F1.wireOp",EDGE,"E2.3"),sQuery(id+"F1.wireOp",EDGE,"E2.4"),sQuery(id+"F1.wireOp",EDGE,"E2.5")])]}),"instanceName":"2"});
            var Q1;
            Q1=makeQuery(id+"F26.opPattern","COPY",BODY,{"derivedFrom":makeQuery(id+"F16.opPattern","COPY",BODY,{"derivedFrom":makeQuery(id+"F15.opPattern","COPY",BODY,{"derivedFrom":makeQuery(id+"F9.opExtrude","SWEPT_BODY",BODY,{"disambiguationData":[OSD([sQuery(id+"F8.wireOp",EDGE,"E7.0"),sQuery(id+"F8.wireOp",EDGE,"E10"),sQuery(id+"F8.wireOp",EDGE,"E11"),sQuery(id+"F8.wireOp",EDGE,"E12.1.0"),sQuery(id+"F8.wireOp",EDGE,"E12.1.1"),sQuery(id+"F8.wireOp",EDGE,"E12.2.0"),sQuery(id+"F8.wireOp",EDGE,"E12.2.1"),sQuery(id+"F8.wireOp",EDGE,"E12.3.0"),sQuery(id+"F8.wireOp",EDGE,"E12.3.1"),sQuery(id+"F8.wireOp",EDGE,"E12.4.0"),sQuery(id+"F8.wireOp",EDGE,"E12.4.1"),sQuery(id+"F8.wireOp",EDGE,"E12.5.0"),sQuery(id+"F8.wireOp",EDGE,"E12.5.1"),sQuery(id+"F8.wireOp",EDGE,"E12.6.0"),sQuery(id+"F8.wireOp",EDGE,"E13"),sQuery(id+"F8.wireOp",EDGE,"E14")])]}),"instanceName":"2"}),"instanceName":"1"}),"instanceName":"2"});
            var Q2;
            Q2=makeQuery(id+"F26.opPattern","COPY",BODY,{"derivedFrom":makeQuery(id+"F13.opPattern","COPY",BODY,{"derivedFrom":makeQuery(id+"F9.opExtrude","SWEPT_BODY",BODY,{"disambiguationData":[OSD([sQuery(id+"F8.wireOp",EDGE,"E7.0"),sQuery(id+"F8.wireOp",EDGE,"E10"),sQuery(id+"F8.wireOp",EDGE,"E11"),sQuery(id+"F8.wireOp",EDGE,"E12.1.0"),sQuery(id+"F8.wireOp",EDGE,"E12.1.1"),sQuery(id+"F8.wireOp",EDGE,"E12.2.0"),sQuery(id+"F8.wireOp",EDGE,"E12.2.1"),sQuery(id+"F8.wireOp",EDGE,"E12.3.0"),sQuery(id+"F8.wireOp",EDGE,"E12.3.1"),sQuery(id+"F8.wireOp",EDGE,"E12.4.0"),sQuery(id+"F8.wireOp",EDGE,"E12.4.1"),sQuery(id+"F8.wireOp",EDGE,"E12.5.0"),sQuery(id+"F8.wireOp",EDGE,"E12.5.1"),sQuery(id+"F8.wireOp",EDGE,"E12.6.0"),sQuery(id+"F8.wireOp",EDGE,"E13"),sQuery(id+"F8.wireOp",EDGE,"E14")])]}),"instanceName":"1"}),"instanceName":"2"});
            var Q3;
            Q3=makeQuery(id+"F18.opPattern","COPY",BODY,{"derivedFrom":makeQuery(id+"F13.opPattern","COPY",BODY,{"derivedFrom":makeQuery(id+"F9.opExtrude","SWEPT_BODY",BODY,{"disambiguationData":[OSD([sQuery(id+"F8.wireOp",EDGE,"E7.0"),sQuery(id+"F8.wireOp",EDGE,"E10"),sQuery(id+"F8.wireOp",EDGE,"E11"),sQuery(id+"F8.wireOp",EDGE,"E12.1.0"),sQuery(id+"F8.wireOp",EDGE,"E12.1.1"),sQuery(id+"F8.wireOp",EDGE,"E12.2.0"),sQuery(id+"F8.wireOp",EDGE,"E12.2.1"),sQuery(id+"F8.wireOp",EDGE,"E12.3.0"),sQuery(id+"F8.wireOp",EDGE,"E12.3.1"),sQuery(id+"F8.wireOp",EDGE,"E12.4.0"),sQuery(id+"F8.wireOp",EDGE,"E12.4.1"),sQuery(id+"F8.wireOp",EDGE,"E12.5.0"),sQuery(id+"F8.wireOp",EDGE,"E12.5.1"),sQuery(id+"F8.wireOp",EDGE,"E12.6.0"),sQuery(id+"F8.wireOp",EDGE,"E13"),sQuery(id+"F8.wireOp",EDGE,"E14")])]}),"instanceName":"2"}),"instanceName":"2"});
            var Q4;
            Q4=sQuery(id+"F55.wireOp",EDGE,"E55");
            circularPattern(context, id + "F56", {"entities" : qUnion([Q0, Q1, Q2, Q3]), "axis" : qUnion([Q4]), "angle" : 120 * degree, "instanceCount" : 2, "oppositeDirection" : true});
        }
        {
            var Q0;
            Q0=makeQuery(id+"F56.opPattern","COPY",FACE,{"derivedFrom":makeQuery(id+"F26.opPattern","COPY",FACE,{"derivedFrom":makeQuery(id+"F3.opExtrude","CAP_FACE",FACE,{"disambiguationData":[OSD([sQuery(id+"F1.wireOp",EDGE,"E2.0"),sQuery(id+"F1.wireOp",EDGE,"E2.1"),sQuery(id+"F1.wireOp",EDGE,"E2.2"),sQuery(id+"F1.wireOp",EDGE,"E2.3"),sQuery(id+"F1.wireOp",EDGE,"E2.4"),sQuery(id+"F1.wireOp",EDGE,"E2.5")])],"isStart":true}),"instanceName":"2"}),"instanceName":"1"});
            var sketch = newSketch(context, id + "F57", { "sketchPlane" : qUnion([Q0])});
            skLineSegment(sketch, "E56", {"start": v(-34.48, 6) * mm, "end": v(-19.62, 8.02) * mm});
            skSolve(sketch);
        }
        {
            var Q0;
            Q0=sQuery(id+"F57.wireOp",VERTEX,"E56.start");
            var Q1;
            Q1=sQuery(id+"F57.wireOp",VERTEX,"E56.end");
            var Q2;
            Q2=makeQuery(id+"F56.opPattern","COPY",VERTEX,{"derivedFrom":makeQuery(id+"F26.opPattern","COPY",VERTEX,{"derivedFrom":makeQuery(id+"F3.opExtrude","CAP_VERTEX",VERTEX,{"disambiguationData":[OSD([sQuery(id+"F1.wireOp",EDGE,"E2.2"),sQuery(id+"F1.wireOp",EDGE,"E2.3")])],"isStart":false}),"instanceName":"2"}),"instanceName":"1"});
            cPlane(context, id + "F58", {"entities" : qUnion([Q0, Q1, Q2]), "cplaneType" : CPlaneType.THREE_POINT, "offset" : 150 * mm, "width" : 150 * mm, "height" : 150 * mm});
        }
        {
            var Q0;
            Q0=qCreatedBy(id+"F58.planeOp",FACE);
            var sketch = newSketch(context, id + "F59", { "sketchPlane" : qUnion([Q0])});
            skLineSegment(sketch, "E57.0", {"start": v(-8.72, -69.64) * mm, "end": v(-20.93, -60.93) * mm});
            skLineSegment(sketch, "E58", {"start": v(-20.93, -60.93) * mm, "end": v(-30.12, -73.8) * mm});
            skSolve(sketch);
        }
        {
            var Q0;
            Q0=makeQuery(id+"F52.opPattern","COPY",BODY,{"derivedFrom":makeQuery(id+"F3.opExtrude","SWEPT_BODY",BODY,{"disambiguationData":[OSD([sQuery(id+"F1.wireOp",EDGE,"E2.0"),sQuery(id+"F1.wireOp",EDGE,"E2.1"),sQuery(id+"F1.wireOp",EDGE,"E2.2"),sQuery(id+"F1.wireOp",EDGE,"E2.3"),sQuery(id+"F1.wireOp",EDGE,"E2.4"),sQuery(id+"F1.wireOp",EDGE,"E2.5")])]}),"instanceName":"1"});
            var Q1;
            Q1=makeQuery(id+"F52.opPattern","COPY",BODY,{"derivedFrom":makeQuery(id+"F16.opPattern","COPY",BODY,{"derivedFrom":makeQuery(id+"F15.opPattern","COPY",BODY,{"derivedFrom":makeQuery(id+"F9.opExtrude","SWEPT_BODY",BODY,{"disambiguationData":[OSD([sQuery(id+"F8.wireOp",EDGE,"E7.0"),sQuery(id+"F8.wireOp",EDGE,"E10"),sQuery(id+"F8.wireOp",EDGE,"E11"),sQuery(id+"F8.wireOp",EDGE,"E12.1.0"),sQuery(id+"F8.wireOp",EDGE,"E12.1.1"),sQuery(id+"F8.wireOp",EDGE,"E12.2.0"),sQuery(id+"F8.wireOp",EDGE,"E12.2.1"),sQuery(id+"F8.wireOp",EDGE,"E12.3.0"),sQuery(id+"F8.wireOp",EDGE,"E12.3.1"),sQuery(id+"F8.wireOp",EDGE,"E12.4.0"),sQuery(id+"F8.wireOp",EDGE,"E12.4.1"),sQuery(id+"F8.wireOp",EDGE,"E12.5.0"),sQuery(id+"F8.wireOp",EDGE,"E12.5.1"),sQuery(id+"F8.wireOp",EDGE,"E12.6.0"),sQuery(id+"F8.wireOp",EDGE,"E13"),sQuery(id+"F8.wireOp",EDGE,"E14")])]}),"instanceName":"2"}),"instanceName":"1"}),"instanceName":"1"});
            var Q2;
            Q2=makeQuery(id+"F52.opPattern","COPY",BODY,{"derivedFrom":makeQuery(id+"F16.opPattern","COPY",BODY,{"derivedFrom":makeQuery(id+"F15.opPattern","COPY",BODY,{"derivedFrom":makeQuery(id+"F9.opExtrude","SWEPT_BODY",BODY,{"disambiguationData":[OSD([sQuery(id+"F8.wireOp",EDGE,"E7.0"),sQuery(id+"F8.wireOp",EDGE,"E10"),sQuery(id+"F8.wireOp",EDGE,"E11"),sQuery(id+"F8.wireOp",EDGE,"E12.1.0"),sQuery(id+"F8.wireOp",EDGE,"E12.1.1"),sQuery(id+"F8.wireOp",EDGE,"E12.2.0"),sQuery(id+"F8.wireOp",EDGE,"E12.2.1"),sQuery(id+"F8.wireOp",EDGE,"E12.3.0"),sQuery(id+"F8.wireOp",EDGE,"E12.3.1"),sQuery(id+"F8.wireOp",EDGE,"E12.4.0"),sQuery(id+"F8.wireOp",EDGE,"E12.4.1"),sQuery(id+"F8.wireOp",EDGE,"E12.5.0"),sQuery(id+"F8.wireOp",EDGE,"E12.5.1"),sQuery(id+"F8.wireOp",EDGE,"E12.6.0"),sQuery(id+"F8.wireOp",EDGE,"E13"),sQuery(id+"F8.wireOp",EDGE,"E14")])]}),"instanceName":"1"}),"instanceName":"1"}),"instanceName":"1"});
            var Q3;
            Q3=makeQuery(id+"F52.opPattern","COPY",BODY,{"derivedFrom":makeQuery(id+"F13.opPattern","COPY",BODY,{"derivedFrom":makeQuery(id+"F9.opExtrude","SWEPT_BODY",BODY,{"disambiguationData":[OSD([sQuery(id+"F8.wireOp",EDGE,"E7.0"),sQuery(id+"F8.wireOp",EDGE,"E10"),sQuery(id+"F8.wireOp",EDGE,"E11"),sQuery(id+"F8.wireOp",EDGE,"E12.1.0"),sQuery(id+"F8.wireOp",EDGE,"E12.1.1"),sQuery(id+"F8.wireOp",EDGE,"E12.2.0"),sQuery(id+"F8.wireOp",EDGE,"E12.2.1"),sQuery(id+"F8.wireOp",EDGE,"E12.3.0"),sQuery(id+"F8.wireOp",EDGE,"E12.3.1"),sQuery(id+"F8.wireOp",EDGE,"E12.4.0"),sQuery(id+"F8.wireOp",EDGE,"E12.4.1"),sQuery(id+"F8.wireOp",EDGE,"E12.5.0"),sQuery(id+"F8.wireOp",EDGE,"E12.5.1"),sQuery(id+"F8.wireOp",EDGE,"E12.6.0"),sQuery(id+"F8.wireOp",EDGE,"E13"),sQuery(id+"F8.wireOp",EDGE,"E14")])]}),"instanceName":"1"}),"instanceName":"1"});
            var Q4;
            Q4=sQuery(id+"F59.wireOp",EDGE,"E58");
            circularPattern(context, id + "F60", {"entities" : qUnion([Q0, Q1, Q2, Q3]), "axis" : qUnion([Q4]), "angle" : 120 * degree, "instanceCount" : 2, "oppositeDirection" : true});
        }
        {
            var Q0;
            Q0=makeQuery(id+"F22.opPattern","COPY",BODY,{"derivedFrom":makeQuery(id+"F17.opPattern","COPY",BODY,{"derivedFrom":makeQuery(id+"F16.opPattern","COPY",BODY,{"derivedFrom":makeQuery(id+"F15.opPattern","COPY",BODY,{"derivedFrom":makeQuery(id+"F9.opExtrude","SWEPT_BODY",BODY,{"disambiguationData":[OSD([sQuery(id+"F8.wireOp",EDGE,"E7.0"),sQuery(id+"F8.wireOp",EDGE,"E10"),sQuery(id+"F8.wireOp",EDGE,"E11"),sQuery(id+"F8.wireOp",EDGE,"E12.1.0"),sQuery(id+"F8.wireOp",EDGE,"E12.1.1"),sQuery(id+"F8.wireOp",EDGE,"E12.2.0"),sQuery(id+"F8.wireOp",EDGE,"E12.2.1"),sQuery(id+"F8.wireOp",EDGE,"E12.3.0"),sQuery(id+"F8.wireOp",EDGE,"E12.3.1"),sQuery(id+"F8.wireOp",EDGE,"E12.4.0"),sQuery(id+"F8.wireOp",EDGE,"E12.4.1"),sQuery(id+"F8.wireOp",EDGE,"E12.5.0"),sQuery(id+"F8.wireOp",EDGE,"E12.5.1"),sQuery(id+"F8.wireOp",EDGE,"E12.6.0"),sQuery(id+"F8.wireOp",EDGE,"E13"),sQuery(id+"F8.wireOp",EDGE,"E14")])]}),"instanceName":"1"}),"instanceName":"1"}),"instanceName":"1"}),"instanceName":"1"});
            deleteBodies(context, id + "F61", {"entities" : qUnion([Q0])});
        }
        {
            var Q0;
            Q0=makeQuery(id+"F22.opPattern","COPY",BODY,{"derivedFrom":makeQuery(id+"F17.opPattern","COPY",BODY,{"derivedFrom":makeQuery(id+"F16.opPattern","COPY",BODY,{"derivedFrom":makeQuery(id+"F15.opPattern","COPY",BODY,{"derivedFrom":makeQuery(id+"F9.opExtrude","SWEPT_BODY",BODY,{"disambiguationData":[OSD([sQuery(id+"F8.wireOp",EDGE,"E7.0"),sQuery(id+"F8.wireOp",EDGE,"E10"),sQuery(id+"F8.wireOp",EDGE,"E11"),sQuery(id+"F8.wireOp",EDGE,"E12.1.0"),sQuery(id+"F8.wireOp",EDGE,"E12.1.1"),sQuery(id+"F8.wireOp",EDGE,"E12.2.0"),sQuery(id+"F8.wireOp",EDGE,"E12.2.1"),sQuery(id+"F8.wireOp",EDGE,"E12.3.0"),sQuery(id+"F8.wireOp",EDGE,"E12.3.1"),sQuery(id+"F8.wireOp",EDGE,"E12.4.0"),sQuery(id+"F8.wireOp",EDGE,"E12.4.1"),sQuery(id+"F8.wireOp",EDGE,"E12.5.0"),sQuery(id+"F8.wireOp",EDGE,"E12.5.1"),sQuery(id+"F8.wireOp",EDGE,"E12.6.0"),sQuery(id+"F8.wireOp",EDGE,"E13"),sQuery(id+"F8.wireOp",EDGE,"E14")])]}),"instanceName":"1"}),"instanceName":"1"}),"instanceName":"1"}),"instanceName":"2"});
            deleteBodies(context, id + "F62", {"entities" : qUnion([Q0])});
        }
        {
            var Q0;
            Q0=makeQuery(id+"F26.opPattern","COPY",BODY,{"derivedFrom":makeQuery(id+"F16.opPattern","COPY",BODY,{"derivedFrom":makeQuery(id+"F15.opPattern","COPY",BODY,{"derivedFrom":makeQuery(id+"F9.opExtrude","SWEPT_BODY",BODY,{"disambiguationData":[OSD([sQuery(id+"F8.wireOp",EDGE,"E7.0"),sQuery(id+"F8.wireOp",EDGE,"E10"),sQuery(id+"F8.wireOp",EDGE,"E11"),sQuery(id+"F8.wireOp",EDGE,"E12.1.0"),sQuery(id+"F8.wireOp",EDGE,"E12.1.1"),sQuery(id+"F8.wireOp",EDGE,"E12.2.0"),sQuery(id+"F8.wireOp",EDGE,"E12.2.1"),sQuery(id+"F8.wireOp",EDGE,"E12.3.0"),sQuery(id+"F8.wireOp",EDGE,"E12.3.1"),sQuery(id+"F8.wireOp",EDGE,"E12.4.0"),sQuery(id+"F8.wireOp",EDGE,"E12.4.1"),sQuery(id+"F8.wireOp",EDGE,"E12.5.0"),sQuery(id+"F8.wireOp",EDGE,"E12.5.1"),sQuery(id+"F8.wireOp",EDGE,"E12.6.0"),sQuery(id+"F8.wireOp",EDGE,"E13"),sQuery(id+"F8.wireOp",EDGE,"E14")])]}),"instanceName":"1"}),"instanceName":"1"}),"instanceName":"1"});
            deleteBodies(context, id + "F63", {"entities" : qUnion([Q0])});
        }
        {
            var Q0;
            Q0=makeQuery(id+"F26.opPattern","COPY",BODY,{"derivedFrom":makeQuery(id+"F16.opPattern","COPY",BODY,{"derivedFrom":makeQuery(id+"F15.opPattern","COPY",BODY,{"derivedFrom":makeQuery(id+"F9.opExtrude","SWEPT_BODY",BODY,{"disambiguationData":[OSD([sQuery(id+"F8.wireOp",EDGE,"E7.0"),sQuery(id+"F8.wireOp",EDGE,"E10"),sQuery(id+"F8.wireOp",EDGE,"E11"),sQuery(id+"F8.wireOp",EDGE,"E12.1.0"),sQuery(id+"F8.wireOp",EDGE,"E12.1.1"),sQuery(id+"F8.wireOp",EDGE,"E12.2.0"),sQuery(id+"F8.wireOp",EDGE,"E12.2.1"),sQuery(id+"F8.wireOp",EDGE,"E12.3.0"),sQuery(id+"F8.wireOp",EDGE,"E12.3.1"),sQuery(id+"F8.wireOp",EDGE,"E12.4.0"),sQuery(id+"F8.wireOp",EDGE,"E12.4.1"),sQuery(id+"F8.wireOp",EDGE,"E12.5.0"),sQuery(id+"F8.wireOp",EDGE,"E12.5.1"),sQuery(id+"F8.wireOp",EDGE,"E12.6.0"),sQuery(id+"F8.wireOp",EDGE,"E13"),sQuery(id+"F8.wireOp",EDGE,"E14")])]}),"instanceName":"1"}),"instanceName":"1"}),"instanceName":"2"});
            deleteBodies(context, id + "F64", {"entities" : qUnion([Q0])});
        }
        {
            var Q0;
            Q0=makeQuery(id+"F2.opExtrude","CAP_FACE",FACE,{"disambiguationData":[OSD([sQuery(id+"F0.wireOp",EDGE,"E0.0"),sQuery(id+"F0.wireOp",EDGE,"E0.1"),sQuery(id+"F0.wireOp",EDGE,"E0.2"),sQuery(id+"F0.wireOp",EDGE,"E0.3"),sQuery(id+"F0.wireOp",EDGE,"E0.4")])],"isStart":true});
            extrude(context, id + "F65", {"entities" : qUnion([Q0]), "operationType" : NewBodyOperationType.ADD, "depth" : 2 * mm, "offsetDistance" : 25 * mm});
        }
    });
